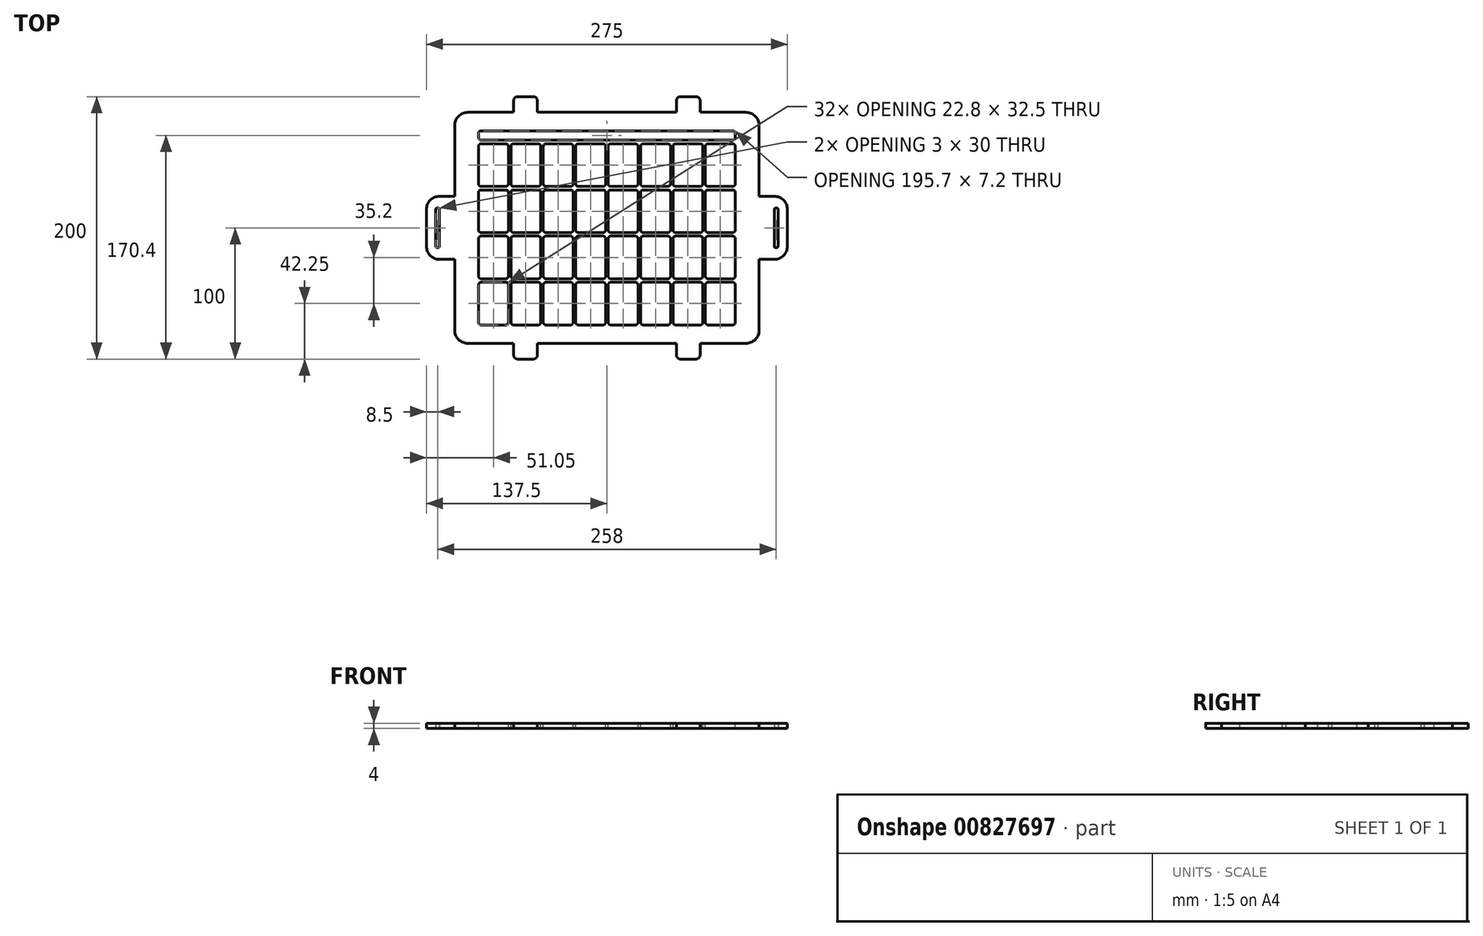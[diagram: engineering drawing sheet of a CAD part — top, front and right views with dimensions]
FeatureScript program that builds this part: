
annotation { "Feature Type Name" : "Feature", "Feature Type Description" : "" }
export const myFeature = defineFeature(function(context is Context, id is Id, definition is map)
    precondition{}
    {
        {
            var Q0;
            Q0=qCreatedBy(makeId("Top.planeOp"),FACE);
            var sketch = newSketch(context, id + "F0", { "sketchPlane" : qUnion([Q0])});
            skLineSegment(sketch, "E0", {"start": v(0, 0) * mm, "end": v(137.5, 0) * mm, "construction": true});
            skLineSegment(sketch, "E1", {"start": v(0, 0) * mm, "end": v(0, 88) * mm, "construction": true});
            skLineSegment(sketch, "E2.MirrorCS", {"start": v(0, 0) * mm, "end": v(0, -88) * mm, "construction": true});
            skLineSegment(sketch, "E3.MirrorCS", {"start": v(0, 0) * mm, "end": v(-137.5, 0) * mm, "construction": true});
            skLineSegment(sketch, "E4.bottom", {"start": v(106, -88) * mm, "end": v(71, -88) * mm});
            skLineSegment(sketch, "E4.top", {"start": v(106, 88) * mm, "end": v(71, 88) * mm});
            skLineSegment(sketch, "E4.left", {"start": v(116, -78) * mm, "end": v(116, -24) * mm});
            skLineSegment(sketch, "E4.right", {"start": v(-116, -78) * mm, "end": v(-116, -24) * mm});
            skPoint(sketch, "E4.middle", {"position": v(0, 0) * mm});
            skLineSegment(sketch, "E5", {"start": v(68, 100) * mm, "end": v(56, 100) * mm});
            skPoint(sketch, "E6.orphan", {"position": v(53, 88) * mm});
            skLineSegment(sketch, "E7", {"start": v(71, 97) * mm, "end": v(71, 88) * mm});
            skLineSegment(sketch, "E8.trimOffspring", {"start": v(53, 88) * mm, "end": v(-53, 88) * mm});
            skLineSegment(sketch, "E9.MirrorCS", {"start": v(68, -100) * mm, "end": v(56, -100) * mm});
            skLineSegment(sketch, "E10.MirrorCS", {"start": v(71, -97) * mm, "end": v(71, -88) * mm});
            skLineSegment(sketch, "E11.trimOffspring", {"start": v(53, -88) * mm, "end": v(-53, -88) * mm});
            skLineSegment(sketch, "E12.MirrorCS", {"start": v(-68, -100) * mm, "end": v(-56, -100) * mm});
            skLineSegment(sketch, "E13.MirrorCS", {"start": v(-71, -97) * mm, "end": v(-71, -88) * mm});
            skLineSegment(sketch, "E14.MirrorCS", {"start": v(-68, 100) * mm, "end": v(-56, 100) * mm});
            skLineSegment(sketch, "E15.MirrorCS", {"start": v(-71, 97) * mm, "end": v(-71, 88) * mm});
            skLineSegment(sketch, "E16", {"start": v(-53, -97) * mm, "end": v(-53, -88) * mm});
            skLineSegment(sketch, "E17.trimOffspring", {"start": v(-71, -88) * mm, "end": v(-106, -88) * mm});
            skLineSegment(sketch, "E18", {"start": v(-53, 97) * mm, "end": v(-53, 88) * mm});
            skLineSegment(sketch, "E19.trimOffspring", {"start": v(-71, 88) * mm, "end": v(-106, 88) * mm});
            skLineSegment(sketch, "E20", {"start": v(53, 97) * mm, "end": v(53, 88) * mm});
            skLineSegment(sketch, "E21", {"start": v(53, -97) * mm, "end": v(53, -88) * mm});
            skPoint(sketch, "E22.visualSharp", {"position": v(-71, 100) * mm});
            skArc(sketch, "E22.filletArc", {"start": v(-68, 100) * mm, "mid": v(-70.12, 99.12) * mm, "end": v(-71, 97) * mm});
            skPoint(sketch, "E23.visualSharp", {"position": v(-53, 100) * mm});
            skArc(sketch, "E23.filletArc", {"start": v(-53, 97) * mm, "mid": v(-53.88, 99.12) * mm, "end": v(-56, 100) * mm});
            skPoint(sketch, "E24.visualSharp", {"position": v(53, 100) * mm});
            skArc(sketch, "E24.filletArc", {"start": v(56, 100) * mm, "mid": v(53.88, 99.12) * mm, "end": v(53, 97) * mm});
            skPoint(sketch, "E25.visualSharp", {"position": v(71, 100) * mm});
            skArc(sketch, "E25.filletArc", {"start": v(71, 97) * mm, "mid": v(70.12, 99.12) * mm, "end": v(68, 100) * mm});
            skPoint(sketch, "E26.visualSharp", {"position": v(-71, -100) * mm});
            skArc(sketch, "E26.filletArc", {"start": v(-71, -97) * mm, "mid": v(-70.12, -99.12) * mm, "end": v(-68, -100) * mm});
            skPoint(sketch, "E27.visualSharp", {"position": v(-53, -100) * mm});
            skArc(sketch, "E27.filletArc", {"start": v(-56, -100) * mm, "mid": v(-53.88, -99.12) * mm, "end": v(-53, -97) * mm});
            skPoint(sketch, "E28.visualSharp", {"position": v(53, -100) * mm});
            skArc(sketch, "E28.filletArc", {"start": v(53, -97) * mm, "mid": v(53.88, -99.12) * mm, "end": v(56, -100) * mm});
            skPoint(sketch, "E29.visualSharp", {"position": v(71, -100) * mm});
            skArc(sketch, "E29.filletArc", {"start": v(68, -100) * mm, "mid": v(70.12, -99.12) * mm, "end": v(71, -97) * mm});
            skLineSegment(sketch, "E30", {"start": v(137.5, -14) * mm, "end": v(137.5, 14) * mm});
            skLineSegment(sketch, "E31", {"start": v(127.5, 24) * mm, "end": v(116, 24) * mm});
            skLineSegment(sketch, "E32.MirrorCS", {"start": v(127.5, -24) * mm, "end": v(116, -24) * mm});
            skPoint(sketch, "E33.orphan", {"position": v(137.5, 53.3) * mm});
            skLineSegment(sketch, "E34.trimOffspring", {"start": v(116, 24) * mm, "end": v(116, 78) * mm});
            skPoint(sketch, "E35.orphan", {"position": v(0, 24) * mm});
            skPoint(sketch, "E36.orphan", {"position": v(0, -24) * mm});
            skPoint(sketch, "E37.visualSharp", {"position": v(137.5, 24) * mm});
            skArc(sketch, "E37.filletArc", {"start": v(137.5, 14) * mm, "mid": v(134.57, 21.07) * mm, "end": v(127.5, 24) * mm});
            skPoint(sketch, "E38.visualSharp", {"position": v(137.5, -24) * mm});
            skArc(sketch, "E38.filletArc", {"start": v(127.5, -24) * mm, "mid": v(134.57, -21.07) * mm, "end": v(137.5, -14) * mm});
            skLineSegment(sketch, "E39", {"start": v(127.5, 15) * mm, "end": v(130.5, 15) * mm});
            skPoint(sketch, "E40.trimOffspring.end.orphan", {"position": v(146.66, 15) * mm});
            skLineSegment(sketch, "E41.MirrorCS", {"start": v(127.5, -15) * mm, "end": v(130.5, -15) * mm});
            skLineSegment(sketch, "E42.MirrorCS", {"start": v(-127.5, 24) * mm, "end": v(-116, 24) * mm});
            skArc(sketch, "E43.MirrorCS", {"start": v(-137.5, 14) * mm, "mid": v(-134.57, 21.07) * mm, "end": v(-127.5, 24) * mm});
            skLineSegment(sketch, "E44.MirrorCS", {"start": v(-137.5, -14) * mm, "end": v(-137.5, 14) * mm});
            skArc(sketch, "E45.MirrorCS", {"start": v(-127.5, -24) * mm, "mid": v(-134.57, -21.07) * mm, "end": v(-137.5, -14) * mm});
            skLineSegment(sketch, "E46.MirrorCS", {"start": v(-127.5, -24) * mm, "end": v(-116, -24) * mm});
            skLineSegment(sketch, "E47.MirrorCS", {"start": v(-127.5, 0) * mm, "end": v(-127.5, 15) * mm});
            skLineSegment(sketch, "E48.MirrorCS", {"start": v(-130.5, 0) * mm, "end": v(-130.5, 15) * mm});
            skLineSegment(sketch, "E49.MirrorCS", {"start": v(-130.5, 0) * mm, "end": v(-130.5, -15) * mm});
            skLineSegment(sketch, "E50.MirrorCS", {"start": v(-127.5, 0) * mm, "end": v(-127.5, -15) * mm});
            skLineSegment(sketch, "E51.MirrorCS", {"start": v(-127.5, 15) * mm, "end": v(-130.5, 15) * mm});
            skLineSegment(sketch, "E52.MirrorCS", {"start": v(-127.5, -15) * mm, "end": v(-130.5, -15) * mm});
            skLineSegment(sketch, "E53.trimOffspring", {"start": v(-116, 24) * mm, "end": v(-116, 78) * mm});
            skPoint(sketch, "E54.visualSharp", {"position": v(-116, 88) * mm});
            skArc(sketch, "E54.filletArc", {"start": v(-106, 88) * mm, "mid": v(-113.07, 85.07) * mm, "end": v(-116, 78) * mm});
            skPoint(sketch, "E55.visualSharp", {"position": v(-116, -88) * mm});
            skArc(sketch, "E55.filletArc", {"start": v(-116, -78) * mm, "mid": v(-113.07, -85.07) * mm, "end": v(-106, -88) * mm});
            skPoint(sketch, "E56.visualSharp", {"position": v(116, -88) * mm});
            skArc(sketch, "E56.filletArc", {"start": v(106, -88) * mm, "mid": v(113.07, -85.07) * mm, "end": v(116, -78) * mm});
            skPoint(sketch, "E57.visualSharp", {"position": v(116, 88) * mm});
            skArc(sketch, "E57.filletArc", {"start": v(116, 78) * mm, "mid": v(113.07, 85.07) * mm, "end": v(106, 88) * mm});
            skLineSegment(sketch, "E58", {"start": v(127.5, -15) * mm, "end": v(127.5, 15) * mm});
            skLineSegment(sketch, "E59", {"start": v(130.5, -15) * mm, "end": v(130.5, 15) * mm});
            skSolve(sketch);
        }
        {
            var Q0;
            Q0=qSketchRegion(id+"F0",true);
            extrude(context, id + "F1", {"entities" : qUnion([Q0]), "depth" : 4 * mm, "offsetDistance" : 25 * mm});
        }
        {
            var Q0;
            Q0=makeQuery(id+"F1.opExtrude","SWEPT_EDGE",EDGE,{"disambiguationData":[OSD([sQuery(id+"F0.wireOp",EDGE,"E41.MirrorCS"),sQuery(id+"F0.wireOp",EDGE,"E58")])]});
            var Q1;
            Q1=makeQuery(id+"F1.opExtrude","SWEPT_EDGE",EDGE,{"disambiguationData":[OSD([sQuery(id+"F0.wireOp",EDGE,"E41.MirrorCS"),sQuery(id+"F0.wireOp",EDGE,"E59")])]});
            fillet(context, id + "F2", {"entities" : qUnion([Q0, Q1]), "radius" : 1 * mm, "tangentPropagation" : true, "allowEdgeOverflow" : false});
        }
        {
            var Q0;
            Q0=makeQuery(id+"F1.opExtrude","SWEPT_EDGE",EDGE,{"disambiguationData":[OSD([sQuery(id+"F0.wireOp",EDGE,"E39"),sQuery(id+"F0.wireOp",EDGE,"E58")])]});
            var Q1;
            Q1=makeQuery(id+"F1.opExtrude","SWEPT_EDGE",EDGE,{"disambiguationData":[OSD([sQuery(id+"F0.wireOp",EDGE,"E39"),sQuery(id+"F0.wireOp",EDGE,"E59")])]});
            fillet(context, id + "F3", {"entities" : qUnion([Q0, Q1]), "radius" : 1 * mm, "tangentPropagation" : true, "allowEdgeOverflow" : false});
        }
        {
            var Q0;
            Q0=makeQuery(id+"F1.opExtrude","SWEPT_EDGE",EDGE,{"disambiguationData":[OSD([sQuery(id+"F0.wireOp",EDGE,"E48.MirrorCS"),sQuery(id+"F0.wireOp",EDGE,"E51.MirrorCS")])]});
            var Q1;
            Q1=makeQuery(id+"F1.opExtrude","SWEPT_EDGE",EDGE,{"disambiguationData":[OSD([sQuery(id+"F0.wireOp",EDGE,"E47.MirrorCS"),sQuery(id+"F0.wireOp",EDGE,"E51.MirrorCS")])]});
            fillet(context, id + "F4", {"entities" : qUnion([Q0, Q1]), "radius" : 1 * mm, "tangentPropagation" : true, "allowEdgeOverflow" : false});
        }
        {
            var Q0;
            Q0=makeQuery(id+"F1.opExtrude","SWEPT_EDGE",EDGE,{"disambiguationData":[OSD([sQuery(id+"F0.wireOp",EDGE,"E49.MirrorCS"),sQuery(id+"F0.wireOp",EDGE,"E52.MirrorCS")])]});
            var Q1;
            Q1=makeQuery(id+"F1.opExtrude","SWEPT_EDGE",EDGE,{"disambiguationData":[OSD([sQuery(id+"F0.wireOp",EDGE,"E50.MirrorCS"),sQuery(id+"F0.wireOp",EDGE,"E52.MirrorCS")])]});
            fillet(context, id + "F5", {"entities" : qUnion([Q0, Q1]), "radius" : 1 * mm, "tangentPropagation" : true, "allowEdgeOverflow" : false});
        }
        {
            var Q0;
            Q0=makeQuery(id+"F1.opExtrude","CAP_FACE",FACE,{"disambiguationData":[OSD([sQuery(id+"F0.wireOp",EDGE,"E4.bottom"),sQuery(id+"F0.wireOp",EDGE,"E4.top"),sQuery(id+"F0.wireOp",EDGE,"E4.left"),sQuery(id+"F0.wireOp",EDGE,"E4.right"),sQuery(id+"F0.wireOp",EDGE,"E5"),sQuery(id+"F0.wireOp",EDGE,"E7"),sQuery(id+"F0.wireOp",EDGE,"E8.trimOffspring"),sQuery(id+"F0.wireOp",EDGE,"E9.MirrorCS"),sQuery(id+"F0.wireOp",EDGE,"E10.MirrorCS"),sQuery(id+"F0.wireOp",EDGE,"E11.trimOffspring"),sQuery(id+"F0.wireOp",EDGE,"E12.MirrorCS"),sQuery(id+"F0.wireOp",EDGE,"E13.MirrorCS"),sQuery(id+"F0.wireOp",EDGE,"E14.MirrorCS"),sQuery(id+"F0.wireOp",EDGE,"E15.MirrorCS"),sQuery(id+"F0.wireOp",EDGE,"E16"),sQuery(id+"F0.wireOp",EDGE,"E17.trimOffspring"),sQuery(id+"F0.wireOp",EDGE,"E18"),sQuery(id+"F0.wireOp",EDGE,"E19.trimOffspring"),sQuery(id+"F0.wireOp",EDGE,"E20"),sQuery(id+"F0.wireOp",EDGE,"E21"),sQuery(id+"F0.wireOp",EDGE,"E22.filletArc"),sQuery(id+"F0.wireOp",EDGE,"E23.filletArc"),sQuery(id+"F0.wireOp",EDGE,"E24.filletArc"),sQuery(id+"F0.wireOp",EDGE,"E25.filletArc"),sQuery(id+"F0.wireOp",EDGE,"E26.filletArc"),sQuery(id+"F0.wireOp",EDGE,"E27.filletArc"),sQuery(id+"F0.wireOp",EDGE,"E28.filletArc"),sQuery(id+"F0.wireOp",EDGE,"E29.filletArc"),sQuery(id+"F0.wireOp",EDGE,"E30"),sQuery(id+"F0.wireOp",EDGE,"E31"),sQuery(id+"F0.wireOp",EDGE,"E32.MirrorCS"),sQuery(id+"F0.wireOp",EDGE,"E34.trimOffspring"),sQuery(id+"F0.wireOp",EDGE,"E37.filletArc"),sQuery(id+"F0.wireOp",EDGE,"E38.filletArc"),sQuery(id+"F0.wireOp",EDGE,"E39"),sQuery(id+"F0.wireOp",EDGE,"E41.MirrorCS"),sQuery(id+"F0.wireOp",EDGE,"E42.MirrorCS"),sQuery(id+"F0.wireOp",EDGE,"E43.MirrorCS"),sQuery(id+"F0.wireOp",EDGE,"E44.MirrorCS"),sQuery(id+"F0.wireOp",EDGE,"E45.MirrorCS"),sQuery(id+"F0.wireOp",EDGE,"E46.MirrorCS"),sQuery(id+"F0.wireOp",EDGE,"E47.MirrorCS"),sQuery(id+"F0.wireOp",EDGE,"E48.MirrorCS"),sQuery(id+"F0.wireOp",EDGE,"E49.MirrorCS"),sQuery(id+"F0.wireOp",EDGE,"E50.MirrorCS"),sQuery(id+"F0.wireOp",EDGE,"E51.MirrorCS"),sQuery(id+"F0.wireOp",EDGE,"E52.MirrorCS"),sQuery(id+"F0.wireOp",EDGE,"E53.trimOffspring"),sQuery(id+"F0.wireOp",EDGE,"E54.filletArc"),sQuery(id+"F0.wireOp",EDGE,"E55.filletArc"),sQuery(id+"F0.wireOp",EDGE,"E56.filletArc"),sQuery(id+"F0.wireOp",EDGE,"E57.filletArc"),sQuery(id+"F0.wireOp",EDGE,"E58"),sQuery(id+"F0.wireOp",EDGE,"E59")])],"isStart":false});
            var sketch = newSketch(context, id + "F6", { "sketchPlane" : qUnion([Q0])});
            skLineSegment(sketch, "E60", {"start": v(-127.5, 0) * mm, "end": v(127.5, 0) * mm, "construction": true});
            skLineSegment(sketch, "E61.bottom", {"start": v(95.85, 74) * mm, "end": v(-95.85, 74) * mm});
            skPoint(sketch, "E61.middle", {"position": v(0, 0) * mm});
            skLineSegment(sketch, "E62.bottom", {"start": v(-95.85, -74) * mm, "end": v(-77.05, -74) * mm});
            skLineSegment(sketch, "E62.top", {"start": v(-95.85, -41.5) * mm, "end": v(-77.05, -41.5) * mm});
            skLineSegment(sketch, "E62.left", {"start": v(-97.85, -72) * mm, "end": v(-97.85, -43.5) * mm});
            skLineSegment(sketch, "E62.right", {"start": v(-75.05, -72) * mm, "end": v(-75.05, -43.5) * mm});
            skPoint(sketch, "E63.visualSharp", {"position": v(-75.05, -41.5) * mm});
            skArc(sketch, "E63.filletArc", {"start": v(-75.05, -43.5) * mm, "mid": v(-75.64, -42.09) * mm, "end": v(-77.05, -41.5) * mm});
            skPoint(sketch, "E64.visualSharp", {"position": v(-75.05, -74) * mm});
            skArc(sketch, "E64.filletArc", {"start": v(-77.05, -74) * mm, "mid": v(-75.64, -73.41) * mm, "end": v(-75.05, -72) * mm});
            skPoint(sketch, "E65.visualSharp", {"position": v(-97.85, -74) * mm});
            skArc(sketch, "E65.filletArc", {"start": v(-97.85, -72) * mm, "mid": v(-97.26, -73.41) * mm, "end": v(-95.85, -74) * mm});
            skPoint(sketch, "E66.visualSharp", {"position": v(-97.85, -41.5) * mm});
            skArc(sketch, "E66.filletArc", {"start": v(-95.85, -41.5) * mm, "mid": v(-97.26, -42.09) * mm, "end": v(-97.85, -43.5) * mm});
            skPoint(sketch, "E67.1.0.0", {"position": v(-50.35, -74) * mm});
            skPoint(sketch, "E67.1.0.1", {"position": v(-73.15, -41.5) * mm});
            skPoint(sketch, "E67.1.0.2", {"position": v(-73.15, -74) * mm});
            skLineSegment(sketch, "E67.1.0.3", {"start": v(-71.15, -74) * mm, "end": v(-52.35, -74) * mm});
            skLineSegment(sketch, "E67.1.0.4", {"start": v(-50.35, -72) * mm, "end": v(-50.35, -43.5) * mm});
            skPoint(sketch, "E67.1.0.5", {"position": v(-50.35, -41.5) * mm});
            skLineSegment(sketch, "E67.1.0.6", {"start": v(-71.15, -41.5) * mm, "end": v(-52.35, -41.5) * mm});
            skLineSegment(sketch, "E67.1.0.7", {"start": v(-73.15, -72) * mm, "end": v(-73.15, -43.5) * mm});
            skPoint(sketch, "E67.1.0.8", {"position": v(-73.15, -74) * mm});
            skArc(sketch, "E67.1.0.9", {"start": v(-52.35, -74) * mm, "mid": v(-50.94, -73.41) * mm, "end": v(-50.35, -72) * mm});
            skArc(sketch, "E67.1.0.10", {"start": v(-50.35, -43.5) * mm, "mid": v(-50.94, -42.09) * mm, "end": v(-52.35, -41.5) * mm});
            skArc(sketch, "E67.1.0.11", {"start": v(-71.15, -41.5) * mm, "mid": v(-72.56, -42.09) * mm, "end": v(-73.15, -43.5) * mm});
            skArc(sketch, "E67.1.0.12", {"start": v(-73.15, -72) * mm, "mid": v(-72.56, -73.41) * mm, "end": v(-71.15, -74) * mm});
            skArc(sketch, "E67.1.0.13", {"start": v(-73.15, -72) * mm, "mid": v(-72.56, -73.41) * mm, "end": v(-71.15, -74) * mm});
            skPoint(sketch, "E67.2.0.0", {"position": v(-25.65, -74) * mm});
            skPoint(sketch, "E67.2.0.1", {"position": v(-48.45, -41.5) * mm});
            skPoint(sketch, "E67.2.0.2", {"position": v(-48.45, -74) * mm});
            skLineSegment(sketch, "E67.2.0.3", {"start": v(-46.45, -74) * mm, "end": v(-27.65, -74) * mm});
            skLineSegment(sketch, "E67.2.0.4", {"start": v(-25.65, -72) * mm, "end": v(-25.65, -43.5) * mm});
            skPoint(sketch, "E67.2.0.5", {"position": v(-25.65, -41.5) * mm});
            skLineSegment(sketch, "E67.2.0.6", {"start": v(-46.45, -41.5) * mm, "end": v(-27.65, -41.5) * mm});
            skLineSegment(sketch, "E67.2.0.7", {"start": v(-48.45, -72) * mm, "end": v(-48.45, -43.5) * mm});
            skPoint(sketch, "E67.2.0.8", {"position": v(-48.45, -74) * mm});
            skArc(sketch, "E67.2.0.9", {"start": v(-27.65, -74) * mm, "mid": v(-26.24, -73.41) * mm, "end": v(-25.65, -72) * mm});
            skArc(sketch, "E67.2.0.10", {"start": v(-25.65, -43.5) * mm, "mid": v(-26.24, -42.09) * mm, "end": v(-27.65, -41.5) * mm});
            skArc(sketch, "E67.2.0.11", {"start": v(-46.45, -41.5) * mm, "mid": v(-47.86, -42.09) * mm, "end": v(-48.45, -43.5) * mm});
            skArc(sketch, "E67.2.0.12", {"start": v(-48.45, -72) * mm, "mid": v(-47.86, -73.41) * mm, "end": v(-46.45, -74) * mm});
            skArc(sketch, "E67.2.0.13", {"start": v(-48.45, -72) * mm, "mid": v(-47.86, -73.41) * mm, "end": v(-46.45, -74) * mm});
            skPoint(sketch, "E67.3.0.0", {"position": v(-0.95, -74) * mm});
            skPoint(sketch, "E67.3.0.1", {"position": v(-23.75, -41.5) * mm});
            skPoint(sketch, "E67.3.0.2", {"position": v(-23.75, -74) * mm});
            skLineSegment(sketch, "E67.3.0.3", {"start": v(-21.75, -74) * mm, "end": v(-2.95, -74) * mm});
            skLineSegment(sketch, "E67.3.0.4", {"start": v(-0.95, -72) * mm, "end": v(-0.95, -43.5) * mm});
            skPoint(sketch, "E67.3.0.5", {"position": v(-0.95, -41.5) * mm});
            skLineSegment(sketch, "E67.3.0.6", {"start": v(-21.75, -41.5) * mm, "end": v(-2.95, -41.5) * mm});
            skLineSegment(sketch, "E67.3.0.7", {"start": v(-23.75, -72) * mm, "end": v(-23.75, -43.5) * mm});
            skPoint(sketch, "E67.3.0.8", {"position": v(-23.75, -74) * mm});
            skArc(sketch, "E67.3.0.9", {"start": v(-2.95, -74) * mm, "mid": v(-1.54, -73.41) * mm, "end": v(-0.95, -72) * mm});
            skArc(sketch, "E67.3.0.10", {"start": v(-0.95, -43.5) * mm, "mid": v(-1.54, -42.09) * mm, "end": v(-2.95, -41.5) * mm});
            skArc(sketch, "E67.3.0.11", {"start": v(-21.75, -41.5) * mm, "mid": v(-23.16, -42.09) * mm, "end": v(-23.75, -43.5) * mm});
            skArc(sketch, "E67.3.0.12", {"start": v(-23.75, -72) * mm, "mid": v(-23.16, -73.41) * mm, "end": v(-21.75, -74) * mm});
            skArc(sketch, "E67.3.0.13", {"start": v(-23.75, -72) * mm, "mid": v(-23.16, -73.41) * mm, "end": v(-21.75, -74) * mm});
            skPoint(sketch, "E67.4.0.0", {"position": v(23.75, -74) * mm});
            skPoint(sketch, "E67.4.0.1", {"position": v(0.95, -41.5) * mm});
            skPoint(sketch, "E67.4.0.2", {"position": v(0.95, -74) * mm});
            skLineSegment(sketch, "E67.4.0.3", {"start": v(2.95, -74) * mm, "end": v(21.75, -74) * mm});
            skLineSegment(sketch, "E67.4.0.4", {"start": v(23.75, -72) * mm, "end": v(23.75, -43.5) * mm});
            skPoint(sketch, "E67.4.0.5", {"position": v(23.75, -41.5) * mm});
            skLineSegment(sketch, "E67.4.0.6", {"start": v(2.95, -41.5) * mm, "end": v(21.75, -41.5) * mm});
            skLineSegment(sketch, "E67.4.0.7", {"start": v(0.95, -72) * mm, "end": v(0.95, -43.5) * mm});
            skPoint(sketch, "E67.4.0.8", {"position": v(0.95, -74) * mm});
            skArc(sketch, "E67.4.0.9", {"start": v(21.75, -74) * mm, "mid": v(23.16, -73.41) * mm, "end": v(23.75, -72) * mm});
            skArc(sketch, "E67.4.0.10", {"start": v(23.75, -43.5) * mm, "mid": v(23.16, -42.09) * mm, "end": v(21.75, -41.5) * mm});
            skArc(sketch, "E67.4.0.11", {"start": v(2.95, -41.5) * mm, "mid": v(1.54, -42.09) * mm, "end": v(0.95, -43.5) * mm});
            skArc(sketch, "E67.4.0.12", {"start": v(0.95, -72) * mm, "mid": v(1.54, -73.41) * mm, "end": v(2.95, -74) * mm});
            skArc(sketch, "E67.4.0.13", {"start": v(0.95, -72) * mm, "mid": v(1.54, -73.41) * mm, "end": v(2.95, -74) * mm});
            skPoint(sketch, "E67.5.0.0", {"position": v(48.45, -74) * mm});
            skPoint(sketch, "E67.5.0.1", {"position": v(25.65, -41.5) * mm});
            skPoint(sketch, "E67.5.0.2", {"position": v(25.65, -74) * mm});
            skLineSegment(sketch, "E67.5.0.3", {"start": v(27.65, -74) * mm, "end": v(46.45, -74) * mm});
            skLineSegment(sketch, "E67.5.0.4", {"start": v(48.45, -72) * mm, "end": v(48.45, -43.5) * mm});
            skPoint(sketch, "E67.5.0.5", {"position": v(48.45, -41.5) * mm});
            skLineSegment(sketch, "E67.5.0.6", {"start": v(27.65, -41.5) * mm, "end": v(46.45, -41.5) * mm});
            skLineSegment(sketch, "E67.5.0.7", {"start": v(25.65, -72) * mm, "end": v(25.65, -43.5) * mm});
            skPoint(sketch, "E67.5.0.8", {"position": v(25.65, -74) * mm});
            skArc(sketch, "E67.5.0.9", {"start": v(46.45, -74) * mm, "mid": v(47.86, -73.41) * mm, "end": v(48.45, -72) * mm});
            skArc(sketch, "E67.5.0.10", {"start": v(48.45, -43.5) * mm, "mid": v(47.86, -42.09) * mm, "end": v(46.45, -41.5) * mm});
            skArc(sketch, "E67.5.0.11", {"start": v(27.65, -41.5) * mm, "mid": v(26.24, -42.09) * mm, "end": v(25.65, -43.5) * mm});
            skArc(sketch, "E67.5.0.12", {"start": v(25.65, -72) * mm, "mid": v(26.24, -73.41) * mm, "end": v(27.65, -74) * mm});
            skArc(sketch, "E67.5.0.13", {"start": v(25.65, -72) * mm, "mid": v(26.24, -73.41) * mm, "end": v(27.65, -74) * mm});
            skPoint(sketch, "E67.6.0.0", {"position": v(73.15, -74) * mm});
            skPoint(sketch, "E67.6.0.1", {"position": v(50.35, -41.5) * mm});
            skPoint(sketch, "E67.6.0.2", {"position": v(50.35, -74) * mm});
            skLineSegment(sketch, "E67.6.0.3", {"start": v(52.35, -74) * mm, "end": v(71.15, -74) * mm});
            skLineSegment(sketch, "E67.6.0.4", {"start": v(73.15, -72) * mm, "end": v(73.15, -43.5) * mm});
            skPoint(sketch, "E67.6.0.5", {"position": v(73.15, -41.5) * mm});
            skLineSegment(sketch, "E67.6.0.6", {"start": v(52.35, -41.5) * mm, "end": v(71.15, -41.5) * mm});
            skLineSegment(sketch, "E67.6.0.7", {"start": v(50.35, -72) * mm, "end": v(50.35, -43.5) * mm});
            skPoint(sketch, "E67.6.0.8", {"position": v(50.35, -74) * mm});
            skArc(sketch, "E67.6.0.9", {"start": v(71.15, -74) * mm, "mid": v(72.56, -73.41) * mm, "end": v(73.15, -72) * mm});
            skArc(sketch, "E67.6.0.10", {"start": v(73.15, -43.5) * mm, "mid": v(72.56, -42.09) * mm, "end": v(71.15, -41.5) * mm});
            skArc(sketch, "E67.6.0.11", {"start": v(52.35, -41.5) * mm, "mid": v(50.94, -42.09) * mm, "end": v(50.35, -43.5) * mm});
            skArc(sketch, "E67.6.0.12", {"start": v(50.35, -72) * mm, "mid": v(50.94, -73.41) * mm, "end": v(52.35, -74) * mm});
            skArc(sketch, "E67.6.0.13", {"start": v(50.35, -72) * mm, "mid": v(50.94, -73.41) * mm, "end": v(52.35, -74) * mm});
            skPoint(sketch, "E67.7.0.0", {"position": v(97.85, -74) * mm});
            skPoint(sketch, "E67.7.0.1", {"position": v(75.05, -41.5) * mm});
            skPoint(sketch, "E67.7.0.2", {"position": v(75.05, -74) * mm});
            skLineSegment(sketch, "E67.7.0.3", {"start": v(77.05, -74) * mm, "end": v(95.85, -74) * mm});
            skLineSegment(sketch, "E67.7.0.4", {"start": v(97.85, -72) * mm, "end": v(97.85, -43.5) * mm});
            skPoint(sketch, "E67.7.0.5", {"position": v(97.85, -41.5) * mm});
            skLineSegment(sketch, "E67.7.0.6", {"start": v(77.05, -41.5) * mm, "end": v(95.85, -41.5) * mm});
            skLineSegment(sketch, "E67.7.0.7", {"start": v(75.05, -72) * mm, "end": v(75.05, -43.5) * mm});
            skPoint(sketch, "E67.7.0.8", {"position": v(75.05, -74) * mm});
            skArc(sketch, "E67.7.0.9", {"start": v(95.85, -74) * mm, "mid": v(97.26, -73.41) * mm, "end": v(97.85, -72) * mm});
            skArc(sketch, "E67.7.0.10", {"start": v(97.85, -43.5) * mm, "mid": v(97.26, -42.09) * mm, "end": v(95.85, -41.5) * mm});
            skArc(sketch, "E67.7.0.11", {"start": v(77.05, -41.5) * mm, "mid": v(75.64, -42.09) * mm, "end": v(75.05, -43.5) * mm});
            skArc(sketch, "E67.7.0.12", {"start": v(75.05, -72) * mm, "mid": v(75.64, -73.41) * mm, "end": v(77.05, -74) * mm});
            skArc(sketch, "E67.7.0.13", {"start": v(75.05, -72) * mm, "mid": v(75.64, -73.41) * mm, "end": v(77.05, -74) * mm});
            skLineSegment(sketch, "E67.direction1", {"start": v(-97.85, -74) * mm, "end": v(-73.15, -74) * mm, "construction": true});
            skLineSegment(sketch, "E68.0.1.0", {"start": v(-25.65, -36.8) * mm, "end": v(-25.65, -8.3) * mm});
            skPoint(sketch, "E68.0.1.1", {"position": v(25.65, -38.8) * mm});
            skLineSegment(sketch, "E68.0.1.2", {"start": v(-75.05, -36.8) * mm, "end": v(-75.05, -8.3) * mm});
            skPoint(sketch, "E68.0.1.3", {"position": v(75.05, -6.3) * mm});
            skPoint(sketch, "E68.0.1.4", {"position": v(-50.35, -38.8) * mm});
            skLineSegment(sketch, "E68.0.1.5", {"start": v(27.65, -6.3) * mm, "end": v(46.45, -6.3) * mm});
            skLineSegment(sketch, "E68.0.1.6", {"start": v(48.45, -36.8) * mm, "end": v(48.45, -8.3) * mm});
            skPoint(sketch, "E68.0.1.7", {"position": v(0.95, -6.3) * mm});
            skPoint(sketch, "E68.0.1.8", {"position": v(-73.15, -38.8) * mm});
            skLineSegment(sketch, "E68.0.1.9", {"start": v(-95.85, -6.3) * mm, "end": v(-77.05, -6.3) * mm});
            skLineSegment(sketch, "E68.0.1.10", {"start": v(-97.85, -36.8) * mm, "end": v(-97.85, -8.3) * mm});
            skLineSegment(sketch, "E68.0.1.11", {"start": v(75.05, -36.8) * mm, "end": v(75.05, -8.3) * mm});
            skLineSegment(sketch, "E68.0.1.12", {"start": v(-21.75, -38.8) * mm, "end": v(-2.95, -38.8) * mm});
            skPoint(sketch, "E68.0.1.13", {"position": v(50.35, -6.3) * mm});
            skPoint(sketch, "E68.0.1.14", {"position": v(97.85, -6.3) * mm});
            skPoint(sketch, "E68.0.1.15", {"position": v(-97.85, -6.3) * mm});
            skLineSegment(sketch, "E68.0.1.16", {"start": v(-23.75, -36.8) * mm, "end": v(-23.75, -8.3) * mm});
            skPoint(sketch, "E68.0.1.17", {"position": v(-0.95, -38.8) * mm});
            skPoint(sketch, "E68.0.1.18", {"position": v(-25.65, -6.3) * mm});
            skPoint(sketch, "E68.0.1.19", {"position": v(-25.65, -38.8) * mm});
            skLineSegment(sketch, "E68.0.1.20", {"start": v(-71.15, -6.3) * mm, "end": v(-52.35, -6.3) * mm});
            skPoint(sketch, "E68.0.1.21", {"position": v(97.85, -38.8) * mm});
            skPoint(sketch, "E68.0.1.22", {"position": v(-75.05, -6.3) * mm});
            skPoint(sketch, "E68.0.1.23", {"position": v(50.35, -38.8) * mm});
            skPoint(sketch, "E68.0.1.24", {"position": v(-48.45, -6.3) * mm});
            skLineSegment(sketch, "E68.0.1.25", {"start": v(2.95, -6.3) * mm, "end": v(21.75, -6.3) * mm});
            skPoint(sketch, "E68.0.1.26", {"position": v(-50.35, -6.3) * mm});
            skLineSegment(sketch, "E68.0.1.27", {"start": v(2.95, -38.8) * mm, "end": v(21.75, -38.8) * mm});
            skLineSegment(sketch, "E68.0.1.28", {"start": v(-73.15, -36.8) * mm, "end": v(-73.15, -8.3) * mm});
            skLineSegment(sketch, "E68.0.1.29", {"start": v(-46.45, -6.3) * mm, "end": v(-27.65, -6.3) * mm});
            skLineSegment(sketch, "E68.0.1.30", {"start": v(23.75, -36.8) * mm, "end": v(23.75, -8.3) * mm});
            skLineSegment(sketch, "E68.0.1.31", {"start": v(50.35, -36.8) * mm, "end": v(50.35, -8.3) * mm});
            skLineSegment(sketch, "E68.0.1.32", {"start": v(-46.45, -38.8) * mm, "end": v(-27.65, -38.8) * mm});
            skPoint(sketch, "E68.0.1.33", {"position": v(48.45, -6.3) * mm});
            skLineSegment(sketch, "E68.0.1.34", {"start": v(52.35, -38.8) * mm, "end": v(71.15, -38.8) * mm});
            skLineSegment(sketch, "E68.0.1.35", {"start": v(-0.95, -36.8) * mm, "end": v(-0.95, -8.3) * mm});
            skLineSegment(sketch, "E68.0.1.36", {"start": v(-48.45, -36.8) * mm, "end": v(-48.45, -8.3) * mm});
            skLineSegment(sketch, "E68.0.1.37", {"start": v(77.05, -6.3) * mm, "end": v(95.85, -6.3) * mm});
            skPoint(sketch, "E68.0.1.38", {"position": v(0.95, -38.8) * mm});
            skPoint(sketch, "E68.0.1.39", {"position": v(25.65, -6.3) * mm});
            skLineSegment(sketch, "E68.0.1.40", {"start": v(52.35, -6.3) * mm, "end": v(71.15, -6.3) * mm});
            skLineSegment(sketch, "E68.0.1.41", {"start": v(97.85, -36.8) * mm, "end": v(97.85, -8.3) * mm});
            skPoint(sketch, "E68.0.1.42", {"position": v(73.15, -38.8) * mm});
            skLineSegment(sketch, "E68.0.1.43", {"start": v(25.65, -36.8) * mm, "end": v(25.65, -8.3) * mm});
            skPoint(sketch, "E68.0.1.44", {"position": v(-73.15, -6.3) * mm});
            skPoint(sketch, "E68.0.1.45", {"position": v(23.75, -6.3) * mm});
            skLineSegment(sketch, "E68.0.1.46", {"start": v(27.65, -38.8) * mm, "end": v(46.45, -38.8) * mm});
            skLineSegment(sketch, "E68.0.1.47", {"start": v(0.95, -36.8) * mm, "end": v(0.95, -8.3) * mm});
            skLineSegment(sketch, "E68.0.1.48", {"start": v(73.15, -36.8) * mm, "end": v(73.15, -8.3) * mm});
            skPoint(sketch, "E68.0.1.49", {"position": v(48.45, -38.8) * mm});
            skPoint(sketch, "E68.0.1.50", {"position": v(-0.95, -6.3) * mm});
            skLineSegment(sketch, "E68.0.1.51", {"start": v(-71.15, -38.8) * mm, "end": v(-52.35, -38.8) * mm});
            skLineSegment(sketch, "E68.0.1.52", {"start": v(-50.35, -36.8) * mm, "end": v(-50.35, -8.3) * mm});
            skLineSegment(sketch, "E68.0.1.53", {"start": v(-21.75, -6.3) * mm, "end": v(-2.95, -6.3) * mm});
            skPoint(sketch, "E68.0.1.54", {"position": v(73.15, -6.3) * mm});
            skPoint(sketch, "E68.0.1.55", {"position": v(23.75, -38.8) * mm});
            skPoint(sketch, "E68.0.1.56", {"position": v(-48.45, -38.8) * mm});
            skPoint(sketch, "E68.0.1.57", {"position": v(-23.75, -6.3) * mm});
            skPoint(sketch, "E68.0.1.58", {"position": v(-97.85, -38.8) * mm});
            skPoint(sketch, "E68.0.1.59", {"position": v(75.05, -38.8) * mm});
            skPoint(sketch, "E68.0.1.60", {"position": v(-23.75, -38.8) * mm});
            skLineSegment(sketch, "E68.0.1.61", {"start": v(77.05, -38.8) * mm, "end": v(95.85, -38.8) * mm});
            skPoint(sketch, "E68.0.1.62", {"position": v(-23.75, -38.8) * mm});
            skPoint(sketch, "E68.0.1.63", {"position": v(25.65, -38.8) * mm});
            skPoint(sketch, "E68.0.1.64", {"position": v(0.95, -38.8) * mm});
            skPoint(sketch, "E68.0.1.65", {"position": v(-97.85, -38.8) * mm});
            skPoint(sketch, "E68.0.1.66", {"position": v(50.35, -38.8) * mm});
            skPoint(sketch, "E68.0.1.67", {"position": v(-48.45, -38.8) * mm});
            skPoint(sketch, "E68.0.1.68", {"position": v(75.05, -38.8) * mm});
            skPoint(sketch, "E68.0.1.69", {"position": v(-73.15, -38.8) * mm});
            skLineSegment(sketch, "E68.0.1.70", {"start": v(-97.85, -38.8) * mm, "end": v(-73.15, -38.8) * mm, "construction": true});
            skPoint(sketch, "E68.0.1.71", {"position": v(-75.05, -38.8) * mm});
            skLineSegment(sketch, "E68.0.1.72", {"start": v(-95.85, -38.8) * mm, "end": v(-77.05, -38.8) * mm});
            skArc(sketch, "E68.0.1.73", {"start": v(-95.85, -6.3) * mm, "mid": v(-97.26, -6.89) * mm, "end": v(-97.85, -8.3) * mm});
            skArc(sketch, "E68.0.1.74", {"start": v(77.05, -6.3) * mm, "mid": v(75.64, -6.89) * mm, "end": v(75.05, -8.3) * mm});
            skArc(sketch, "E68.0.1.75", {"start": v(95.85, -38.8) * mm, "mid": v(97.26, -38.21) * mm, "end": v(97.85, -36.8) * mm});
            skArc(sketch, "E68.0.1.76", {"start": v(-71.15, -6.3) * mm, "mid": v(-72.56, -6.89) * mm, "end": v(-73.15, -8.3) * mm});
            skArc(sketch, "E68.0.1.77", {"start": v(-75.05, -8.3) * mm, "mid": v(-75.64, -6.89) * mm, "end": v(-77.05, -6.3) * mm});
            skArc(sketch, "E68.0.1.78", {"start": v(73.15, -8.3) * mm, "mid": v(72.56, -6.89) * mm, "end": v(71.15, -6.3) * mm});
            skArc(sketch, "E68.0.1.79", {"start": v(-50.35, -8.3) * mm, "mid": v(-50.94, -6.89) * mm, "end": v(-52.35, -6.3) * mm});
            skArc(sketch, "E68.0.1.80", {"start": v(-46.45, -6.3) * mm, "mid": v(-47.86, -6.89) * mm, "end": v(-48.45, -8.3) * mm});
            skArc(sketch, "E68.0.1.81", {"start": v(97.85, -8.3) * mm, "mid": v(97.26, -6.89) * mm, "end": v(95.85, -6.3) * mm});
            skArc(sketch, "E68.0.1.82", {"start": v(23.75, -8.3) * mm, "mid": v(23.16, -6.89) * mm, "end": v(21.75, -6.3) * mm});
            skArc(sketch, "E68.0.1.83", {"start": v(48.45, -8.3) * mm, "mid": v(47.86, -6.89) * mm, "end": v(46.45, -6.3) * mm});
            skArc(sketch, "E68.0.1.84", {"start": v(27.65, -6.3) * mm, "mid": v(26.24, -6.89) * mm, "end": v(25.65, -8.3) * mm});
            skArc(sketch, "E68.0.1.85", {"start": v(52.35, -6.3) * mm, "mid": v(50.94, -6.89) * mm, "end": v(50.35, -8.3) * mm});
            skArc(sketch, "E68.0.1.86", {"start": v(-21.75, -6.3) * mm, "mid": v(-23.16, -6.89) * mm, "end": v(-23.75, -8.3) * mm});
            skArc(sketch, "E68.0.1.87", {"start": v(-0.95, -8.3) * mm, "mid": v(-1.54, -6.89) * mm, "end": v(-2.95, -6.3) * mm});
            skArc(sketch, "E68.0.1.88", {"start": v(-25.65, -8.3) * mm, "mid": v(-26.24, -6.89) * mm, "end": v(-27.65, -6.3) * mm});
            skArc(sketch, "E68.0.1.89", {"start": v(2.95, -6.3) * mm, "mid": v(1.54, -6.89) * mm, "end": v(0.95, -8.3) * mm});
            skArc(sketch, "E68.0.1.90", {"start": v(-77.05, -38.8) * mm, "mid": v(-75.64, -38.21) * mm, "end": v(-75.05, -36.8) * mm});
            skArc(sketch, "E68.0.1.91", {"start": v(50.35, -36.8) * mm, "mid": v(50.94, -38.21) * mm, "end": v(52.35, -38.8) * mm});
            skArc(sketch, "E68.0.1.92", {"start": v(-52.35, -38.8) * mm, "mid": v(-50.94, -38.21) * mm, "end": v(-50.35, -36.8) * mm});
            skArc(sketch, "E68.0.1.93", {"start": v(0.95, -36.8) * mm, "mid": v(1.54, -38.21) * mm, "end": v(2.95, -38.8) * mm});
            skArc(sketch, "E68.0.1.94", {"start": v(46.45, -38.8) * mm, "mid": v(47.86, -38.21) * mm, "end": v(48.45, -36.8) * mm});
            skArc(sketch, "E68.0.1.95", {"start": v(-73.15, -36.8) * mm, "mid": v(-72.56, -38.21) * mm, "end": v(-71.15, -38.8) * mm});
            skArc(sketch, "E68.0.1.96", {"start": v(-97.85, -36.8) * mm, "mid": v(-97.26, -38.21) * mm, "end": v(-95.85, -38.8) * mm});
            skArc(sketch, "E68.0.1.97", {"start": v(-48.45, -36.8) * mm, "mid": v(-47.86, -38.21) * mm, "end": v(-46.45, -38.8) * mm});
            skArc(sketch, "E68.0.1.98", {"start": v(-2.95, -38.8) * mm, "mid": v(-1.54, -38.21) * mm, "end": v(-0.95, -36.8) * mm});
            skArc(sketch, "E68.0.1.99", {"start": v(-48.45, -36.8) * mm, "mid": v(-47.86, -38.21) * mm, "end": v(-46.45, -38.8) * mm});
            skArc(sketch, "E68.0.1.100", {"start": v(-27.65, -38.8) * mm, "mid": v(-26.24, -38.21) * mm, "end": v(-25.65, -36.8) * mm});
            skArc(sketch, "E68.0.1.101", {"start": v(-23.75, -36.8) * mm, "mid": v(-23.16, -38.21) * mm, "end": v(-21.75, -38.8) * mm});
            skArc(sketch, "E68.0.1.102", {"start": v(0.95, -36.8) * mm, "mid": v(1.54, -38.21) * mm, "end": v(2.95, -38.8) * mm});
            skArc(sketch, "E68.0.1.103", {"start": v(50.35, -36.8) * mm, "mid": v(50.94, -38.21) * mm, "end": v(52.35, -38.8) * mm});
            skArc(sketch, "E68.0.1.104", {"start": v(-73.15, -36.8) * mm, "mid": v(-72.56, -38.21) * mm, "end": v(-71.15, -38.8) * mm});
            skArc(sketch, "E68.0.1.105", {"start": v(-97.85, -36.8) * mm, "mid": v(-97.26, -38.21) * mm, "end": v(-95.85, -38.8) * mm});
            skArc(sketch, "E68.0.1.106", {"start": v(-23.75, -36.8) * mm, "mid": v(-23.16, -38.21) * mm, "end": v(-21.75, -38.8) * mm});
            skArc(sketch, "E68.0.1.107", {"start": v(25.65, -36.8) * mm, "mid": v(26.24, -38.21) * mm, "end": v(27.65, -38.8) * mm});
            skArc(sketch, "E68.0.1.108", {"start": v(21.75, -38.8) * mm, "mid": v(23.16, -38.21) * mm, "end": v(23.75, -36.8) * mm});
            skArc(sketch, "E68.0.1.109", {"start": v(75.05, -36.8) * mm, "mid": v(75.64, -38.21) * mm, "end": v(77.05, -38.8) * mm});
            skArc(sketch, "E68.0.1.110", {"start": v(71.15, -38.8) * mm, "mid": v(72.56, -38.21) * mm, "end": v(73.15, -36.8) * mm});
            skArc(sketch, "E68.0.1.111", {"start": v(25.65, -36.8) * mm, "mid": v(26.24, -38.21) * mm, "end": v(27.65, -38.8) * mm});
            skArc(sketch, "E68.0.1.112", {"start": v(75.05, -36.8) * mm, "mid": v(75.64, -38.21) * mm, "end": v(77.05, -38.8) * mm});
            skLineSegment(sketch, "E68.0.2.0", {"start": v(-25.65, -1.6) * mm, "end": v(-25.65, 26.9) * mm});
            skPoint(sketch, "E68.0.2.1", {"position": v(25.65, -3.6) * mm});
            skLineSegment(sketch, "E68.0.2.2", {"start": v(-75.05, -1.6) * mm, "end": v(-75.05, 26.9) * mm});
            skPoint(sketch, "E68.0.2.3", {"position": v(75.05, 28.9) * mm});
            skPoint(sketch, "E68.0.2.4", {"position": v(-50.35, -3.6) * mm});
            skLineSegment(sketch, "E68.0.2.5", {"start": v(27.65, 28.9) * mm, "end": v(46.45, 28.9) * mm});
            skLineSegment(sketch, "E68.0.2.6", {"start": v(48.45, -1.6) * mm, "end": v(48.45, 26.9) * mm});
            skPoint(sketch, "E68.0.2.7", {"position": v(0.95, 28.9) * mm});
            skPoint(sketch, "E68.0.2.8", {"position": v(-73.15, -3.6) * mm});
            skLineSegment(sketch, "E68.0.2.9", {"start": v(-95.85, 28.9) * mm, "end": v(-77.05, 28.9) * mm});
            skLineSegment(sketch, "E68.0.2.10", {"start": v(-97.85, -1.6) * mm, "end": v(-97.85, 26.9) * mm});
            skLineSegment(sketch, "E68.0.2.11", {"start": v(75.05, -1.6) * mm, "end": v(75.05, 26.9) * mm});
            skLineSegment(sketch, "E68.0.2.12", {"start": v(-21.75, -3.6) * mm, "end": v(-2.95, -3.6) * mm});
            skPoint(sketch, "E68.0.2.13", {"position": v(50.35, 28.9) * mm});
            skPoint(sketch, "E68.0.2.14", {"position": v(97.85, 28.9) * mm});
            skPoint(sketch, "E68.0.2.15", {"position": v(-97.85, 28.9) * mm});
            skLineSegment(sketch, "E68.0.2.16", {"start": v(-23.75, -1.6) * mm, "end": v(-23.75, 26.9) * mm});
            skPoint(sketch, "E68.0.2.17", {"position": v(-0.95, -3.6) * mm});
            skPoint(sketch, "E68.0.2.18", {"position": v(-25.65, 28.9) * mm});
            skPoint(sketch, "E68.0.2.19", {"position": v(-25.65, -3.6) * mm});
            skLineSegment(sketch, "E68.0.2.20", {"start": v(-71.15, 28.9) * mm, "end": v(-52.35, 28.9) * mm});
            skPoint(sketch, "E68.0.2.21", {"position": v(97.85, -3.6) * mm});
            skPoint(sketch, "E68.0.2.22", {"position": v(-75.05, 28.9) * mm});
            skPoint(sketch, "E68.0.2.23", {"position": v(50.35, -3.6) * mm});
            skPoint(sketch, "E68.0.2.24", {"position": v(-48.45, 28.9) * mm});
            skLineSegment(sketch, "E68.0.2.25", {"start": v(2.95, 28.9) * mm, "end": v(21.75, 28.9) * mm});
            skPoint(sketch, "E68.0.2.26", {"position": v(-50.35, 28.9) * mm});
            skLineSegment(sketch, "E68.0.2.27", {"start": v(2.95, -3.6) * mm, "end": v(21.75, -3.6) * mm});
            skLineSegment(sketch, "E68.0.2.28", {"start": v(-73.15, -1.6) * mm, "end": v(-73.15, 26.9) * mm});
            skLineSegment(sketch, "E68.0.2.29", {"start": v(-46.45, 28.9) * mm, "end": v(-27.65, 28.9) * mm});
            skLineSegment(sketch, "E68.0.2.30", {"start": v(23.75, -1.6) * mm, "end": v(23.75, 26.9) * mm});
            skLineSegment(sketch, "E68.0.2.31", {"start": v(50.35, -1.6) * mm, "end": v(50.35, 26.9) * mm});
            skLineSegment(sketch, "E68.0.2.32", {"start": v(-46.45, -3.6) * mm, "end": v(-27.65, -3.6) * mm});
            skPoint(sketch, "E68.0.2.33", {"position": v(48.45, 28.9) * mm});
            skLineSegment(sketch, "E68.0.2.34", {"start": v(52.35, -3.6) * mm, "end": v(71.15, -3.6) * mm});
            skLineSegment(sketch, "E68.0.2.35", {"start": v(-0.95, -1.6) * mm, "end": v(-0.95, 26.9) * mm});
            skLineSegment(sketch, "E68.0.2.36", {"start": v(-48.45, -1.6) * mm, "end": v(-48.45, 26.9) * mm});
            skLineSegment(sketch, "E68.0.2.37", {"start": v(77.05, 28.9) * mm, "end": v(95.85, 28.9) * mm});
            skPoint(sketch, "E68.0.2.38", {"position": v(0.95, -3.6) * mm});
            skPoint(sketch, "E68.0.2.39", {"position": v(25.65, 28.9) * mm});
            skLineSegment(sketch, "E68.0.2.40", {"start": v(52.35, 28.9) * mm, "end": v(71.15, 28.9) * mm});
            skLineSegment(sketch, "E68.0.2.41", {"start": v(97.85, -1.6) * mm, "end": v(97.85, 26.9) * mm});
            skPoint(sketch, "E68.0.2.42", {"position": v(73.15, -3.6) * mm});
            skLineSegment(sketch, "E68.0.2.43", {"start": v(25.65, -1.6) * mm, "end": v(25.65, 26.9) * mm});
            skPoint(sketch, "E68.0.2.44", {"position": v(-73.15, 28.9) * mm});
            skPoint(sketch, "E68.0.2.45", {"position": v(23.75, 28.9) * mm});
            skLineSegment(sketch, "E68.0.2.46", {"start": v(27.65, -3.6) * mm, "end": v(46.45, -3.6) * mm});
            skLineSegment(sketch, "E68.0.2.47", {"start": v(0.95, -1.6) * mm, "end": v(0.95, 26.9) * mm});
            skLineSegment(sketch, "E68.0.2.48", {"start": v(73.15, -1.6) * mm, "end": v(73.15, 26.9) * mm});
            skPoint(sketch, "E68.0.2.49", {"position": v(48.45, -3.6) * mm});
            skPoint(sketch, "E68.0.2.50", {"position": v(-0.95, 28.9) * mm});
            skLineSegment(sketch, "E68.0.2.51", {"start": v(-71.15, -3.6) * mm, "end": v(-52.35, -3.6) * mm});
            skLineSegment(sketch, "E68.0.2.52", {"start": v(-50.35, -1.6) * mm, "end": v(-50.35, 26.9) * mm});
            skLineSegment(sketch, "E68.0.2.53", {"start": v(-21.75, 28.9) * mm, "end": v(-2.95, 28.9) * mm});
            skPoint(sketch, "E68.0.2.54", {"position": v(73.15, 28.9) * mm});
            skPoint(sketch, "E68.0.2.55", {"position": v(23.75, -3.6) * mm});
            skPoint(sketch, "E68.0.2.56", {"position": v(-48.45, -3.6) * mm});
            skPoint(sketch, "E68.0.2.57", {"position": v(-23.75, 28.9) * mm});
            skPoint(sketch, "E68.0.2.58", {"position": v(-97.85, -3.6) * mm});
            skPoint(sketch, "E68.0.2.59", {"position": v(75.05, -3.6) * mm});
            skPoint(sketch, "E68.0.2.60", {"position": v(-23.75, -3.6) * mm});
            skLineSegment(sketch, "E68.0.2.61", {"start": v(77.05, -3.6) * mm, "end": v(95.85, -3.6) * mm});
            skPoint(sketch, "E68.0.2.62", {"position": v(-23.75, -3.6) * mm});
            skPoint(sketch, "E68.0.2.63", {"position": v(25.65, -3.6) * mm});
            skPoint(sketch, "E68.0.2.64", {"position": v(0.95, -3.6) * mm});
            skPoint(sketch, "E68.0.2.65", {"position": v(-97.85, -3.6) * mm});
            skPoint(sketch, "E68.0.2.66", {"position": v(50.35, -3.6) * mm});
            skPoint(sketch, "E68.0.2.67", {"position": v(-48.45, -3.6) * mm});
            skPoint(sketch, "E68.0.2.68", {"position": v(75.05, -3.6) * mm});
            skPoint(sketch, "E68.0.2.69", {"position": v(-73.15, -3.6) * mm});
            skLineSegment(sketch, "E68.0.2.70", {"start": v(-97.85, -3.6) * mm, "end": v(-73.15, -3.6) * mm, "construction": true});
            skPoint(sketch, "E68.0.2.71", {"position": v(-75.05, -3.6) * mm});
            skLineSegment(sketch, "E68.0.2.72", {"start": v(-95.85, -3.6) * mm, "end": v(-77.05, -3.6) * mm});
            skArc(sketch, "E68.0.2.73", {"start": v(-95.85, 28.9) * mm, "mid": v(-97.26, 28.31) * mm, "end": v(-97.85, 26.9) * mm});
            skArc(sketch, "E68.0.2.74", {"start": v(77.05, 28.9) * mm, "mid": v(75.64, 28.31) * mm, "end": v(75.05, 26.9) * mm});
            skArc(sketch, "E68.0.2.75", {"start": v(95.85, -3.6) * mm, "mid": v(97.26, -3.01) * mm, "end": v(97.85, -1.6) * mm});
            skArc(sketch, "E68.0.2.76", {"start": v(-71.15, 28.9) * mm, "mid": v(-72.56, 28.31) * mm, "end": v(-73.15, 26.9) * mm});
            skArc(sketch, "E68.0.2.77", {"start": v(-75.05, 26.9) * mm, "mid": v(-75.64, 28.31) * mm, "end": v(-77.05, 28.9) * mm});
            skArc(sketch, "E68.0.2.78", {"start": v(73.15, 26.9) * mm, "mid": v(72.56, 28.31) * mm, "end": v(71.15, 28.9) * mm});
            skArc(sketch, "E68.0.2.79", {"start": v(-50.35, 26.9) * mm, "mid": v(-50.94, 28.31) * mm, "end": v(-52.35, 28.9) * mm});
            skArc(sketch, "E68.0.2.80", {"start": v(-46.45, 28.9) * mm, "mid": v(-47.86, 28.31) * mm, "end": v(-48.45, 26.9) * mm});
            skArc(sketch, "E68.0.2.81", {"start": v(97.85, 26.9) * mm, "mid": v(97.26, 28.31) * mm, "end": v(95.85, 28.9) * mm});
            skArc(sketch, "E68.0.2.82", {"start": v(23.75, 26.9) * mm, "mid": v(23.16, 28.31) * mm, "end": v(21.75, 28.9) * mm});
            skArc(sketch, "E68.0.2.83", {"start": v(48.45, 26.9) * mm, "mid": v(47.86, 28.31) * mm, "end": v(46.45, 28.9) * mm});
            skArc(sketch, "E68.0.2.84", {"start": v(27.65, 28.9) * mm, "mid": v(26.24, 28.31) * mm, "end": v(25.65, 26.9) * mm});
            skArc(sketch, "E68.0.2.85", {"start": v(52.35, 28.9) * mm, "mid": v(50.94, 28.31) * mm, "end": v(50.35, 26.9) * mm});
            skArc(sketch, "E68.0.2.86", {"start": v(-21.75, 28.9) * mm, "mid": v(-23.16, 28.31) * mm, "end": v(-23.75, 26.9) * mm});
            skArc(sketch, "E68.0.2.87", {"start": v(-0.95, 26.9) * mm, "mid": v(-1.54, 28.31) * mm, "end": v(-2.95, 28.9) * mm});
            skArc(sketch, "E68.0.2.88", {"start": v(-25.65, 26.9) * mm, "mid": v(-26.24, 28.31) * mm, "end": v(-27.65, 28.9) * mm});
            skArc(sketch, "E68.0.2.89", {"start": v(2.95, 28.9) * mm, "mid": v(1.54, 28.31) * mm, "end": v(0.95, 26.9) * mm});
            skArc(sketch, "E68.0.2.90", {"start": v(-77.05, -3.6) * mm, "mid": v(-75.64, -3.01) * mm, "end": v(-75.05, -1.6) * mm});
            skArc(sketch, "E68.0.2.91", {"start": v(50.35, -1.6) * mm, "mid": v(50.94, -3.01) * mm, "end": v(52.35, -3.6) * mm});
            skArc(sketch, "E68.0.2.92", {"start": v(-52.35, -3.6) * mm, "mid": v(-50.94, -3.01) * mm, "end": v(-50.35, -1.6) * mm});
            skArc(sketch, "E68.0.2.93", {"start": v(0.95, -1.6) * mm, "mid": v(1.54, -3.01) * mm, "end": v(2.95, -3.6) * mm});
            skArc(sketch, "E68.0.2.94", {"start": v(46.45, -3.6) * mm, "mid": v(47.86, -3.01) * mm, "end": v(48.45, -1.6) * mm});
            skArc(sketch, "E68.0.2.95", {"start": v(-73.15, -1.6) * mm, "mid": v(-72.56, -3.01) * mm, "end": v(-71.15, -3.6) * mm});
            skArc(sketch, "E68.0.2.96", {"start": v(-97.85, -1.6) * mm, "mid": v(-97.26, -3.01) * mm, "end": v(-95.85, -3.6) * mm});
            skArc(sketch, "E68.0.2.97", {"start": v(-48.45, -1.6) * mm, "mid": v(-47.86, -3.01) * mm, "end": v(-46.45, -3.6) * mm});
            skArc(sketch, "E68.0.2.98", {"start": v(-2.95, -3.6) * mm, "mid": v(-1.54, -3.01) * mm, "end": v(-0.95, -1.6) * mm});
            skArc(sketch, "E68.0.2.99", {"start": v(-48.45, -1.6) * mm, "mid": v(-47.86, -3.01) * mm, "end": v(-46.45, -3.6) * mm});
            skArc(sketch, "E68.0.2.100", {"start": v(-27.65, -3.6) * mm, "mid": v(-26.24, -3.01) * mm, "end": v(-25.65, -1.6) * mm});
            skArc(sketch, "E68.0.2.101", {"start": v(-23.75, -1.6) * mm, "mid": v(-23.16, -3.01) * mm, "end": v(-21.75, -3.6) * mm});
            skArc(sketch, "E68.0.2.102", {"start": v(0.95, -1.6) * mm, "mid": v(1.54, -3.01) * mm, "end": v(2.95, -3.6) * mm});
            skArc(sketch, "E68.0.2.103", {"start": v(50.35, -1.6) * mm, "mid": v(50.94, -3.01) * mm, "end": v(52.35, -3.6) * mm});
            skArc(sketch, "E68.0.2.104", {"start": v(-73.15, -1.6) * mm, "mid": v(-72.56, -3.01) * mm, "end": v(-71.15, -3.6) * mm});
            skArc(sketch, "E68.0.2.105", {"start": v(-97.85, -1.6) * mm, "mid": v(-97.26, -3.01) * mm, "end": v(-95.85, -3.6) * mm});
            skArc(sketch, "E68.0.2.106", {"start": v(-23.75, -1.6) * mm, "mid": v(-23.16, -3.01) * mm, "end": v(-21.75, -3.6) * mm});
            skArc(sketch, "E68.0.2.107", {"start": v(25.65, -1.6) * mm, "mid": v(26.24, -3.01) * mm, "end": v(27.65, -3.6) * mm});
            skArc(sketch, "E68.0.2.108", {"start": v(21.75, -3.6) * mm, "mid": v(23.16, -3.01) * mm, "end": v(23.75, -1.6) * mm});
            skArc(sketch, "E68.0.2.109", {"start": v(75.05, -1.6) * mm, "mid": v(75.64, -3.01) * mm, "end": v(77.05, -3.6) * mm});
            skArc(sketch, "E68.0.2.110", {"start": v(71.15, -3.6) * mm, "mid": v(72.56, -3.01) * mm, "end": v(73.15, -1.6) * mm});
            skArc(sketch, "E68.0.2.111", {"start": v(25.65, -1.6) * mm, "mid": v(26.24, -3.01) * mm, "end": v(27.65, -3.6) * mm});
            skArc(sketch, "E68.0.2.112", {"start": v(75.05, -1.6) * mm, "mid": v(75.64, -3.01) * mm, "end": v(77.05, -3.6) * mm});
            skLineSegment(sketch, "E68.0.3.0", {"start": v(-25.65, 33.6) * mm, "end": v(-25.65, 62.1) * mm});
            skPoint(sketch, "E68.0.3.1", {"position": v(25.65, 31.6) * mm});
            skLineSegment(sketch, "E68.0.3.2", {"start": v(-75.05, 33.6) * mm, "end": v(-75.05, 62.1) * mm});
            skPoint(sketch, "E68.0.3.3", {"position": v(75.05, 64.1) * mm});
            skPoint(sketch, "E68.0.3.4", {"position": v(-50.35, 31.6) * mm});
            skLineSegment(sketch, "E68.0.3.5", {"start": v(27.65, 64.1) * mm, "end": v(46.45, 64.1) * mm});
            skLineSegment(sketch, "E68.0.3.6", {"start": v(48.45, 33.6) * mm, "end": v(48.45, 62.1) * mm});
            skPoint(sketch, "E68.0.3.7", {"position": v(0.95, 64.1) * mm});
            skPoint(sketch, "E68.0.3.8", {"position": v(-73.15, 31.6) * mm});
            skLineSegment(sketch, "E68.0.3.9", {"start": v(-95.85, 64.1) * mm, "end": v(-77.05, 64.1) * mm});
            skLineSegment(sketch, "E68.0.3.10", {"start": v(-97.85, 33.6) * mm, "end": v(-97.85, 62.1) * mm});
            skLineSegment(sketch, "E68.0.3.11", {"start": v(75.05, 33.6) * mm, "end": v(75.05, 62.1) * mm});
            skLineSegment(sketch, "E68.0.3.12", {"start": v(-21.75, 31.6) * mm, "end": v(-2.95, 31.6) * mm});
            skPoint(sketch, "E68.0.3.13", {"position": v(50.35, 64.1) * mm});
            skPoint(sketch, "E68.0.3.14", {"position": v(97.85, 64.1) * mm});
            skPoint(sketch, "E68.0.3.15", {"position": v(-97.85, 64.1) * mm});
            skLineSegment(sketch, "E68.0.3.16", {"start": v(-23.75, 33.6) * mm, "end": v(-23.75, 62.1) * mm});
            skPoint(sketch, "E68.0.3.17", {"position": v(-0.95, 31.6) * mm});
            skPoint(sketch, "E68.0.3.18", {"position": v(-25.65, 64.1) * mm});
            skPoint(sketch, "E68.0.3.19", {"position": v(-25.65, 31.6) * mm});
            skLineSegment(sketch, "E68.0.3.20", {"start": v(-71.15, 64.1) * mm, "end": v(-52.35, 64.1) * mm});
            skPoint(sketch, "E68.0.3.21", {"position": v(97.85, 31.6) * mm});
            skPoint(sketch, "E68.0.3.22", {"position": v(-75.05, 64.1) * mm});
            skPoint(sketch, "E68.0.3.23", {"position": v(50.35, 31.6) * mm});
            skPoint(sketch, "E68.0.3.24", {"position": v(-48.45, 64.1) * mm});
            skLineSegment(sketch, "E68.0.3.25", {"start": v(2.95, 64.1) * mm, "end": v(21.75, 64.1) * mm});
            skPoint(sketch, "E68.0.3.26", {"position": v(-50.35, 64.1) * mm});
            skLineSegment(sketch, "E68.0.3.27", {"start": v(2.95, 31.6) * mm, "end": v(21.75, 31.6) * mm});
            skLineSegment(sketch, "E68.0.3.28", {"start": v(-73.15, 33.6) * mm, "end": v(-73.15, 62.1) * mm});
            skLineSegment(sketch, "E68.0.3.29", {"start": v(-46.45, 64.1) * mm, "end": v(-27.65, 64.1) * mm});
            skLineSegment(sketch, "E68.0.3.30", {"start": v(23.75, 33.6) * mm, "end": v(23.75, 62.1) * mm});
            skLineSegment(sketch, "E68.0.3.31", {"start": v(50.35, 33.6) * mm, "end": v(50.35, 62.1) * mm});
            skLineSegment(sketch, "E68.0.3.32", {"start": v(-46.45, 31.6) * mm, "end": v(-27.65, 31.6) * mm});
            skPoint(sketch, "E68.0.3.33", {"position": v(48.45, 64.1) * mm});
            skLineSegment(sketch, "E68.0.3.34", {"start": v(52.35, 31.6) * mm, "end": v(71.15, 31.6) * mm});
            skLineSegment(sketch, "E68.0.3.35", {"start": v(-0.95, 33.6) * mm, "end": v(-0.95, 62.1) * mm});
            skLineSegment(sketch, "E68.0.3.36", {"start": v(-48.45, 33.6) * mm, "end": v(-48.45, 62.1) * mm});
            skLineSegment(sketch, "E68.0.3.37", {"start": v(77.05, 64.1) * mm, "end": v(95.85, 64.1) * mm});
            skPoint(sketch, "E68.0.3.38", {"position": v(0.95, 31.6) * mm});
            skPoint(sketch, "E68.0.3.39", {"position": v(25.65, 64.1) * mm});
            skLineSegment(sketch, "E68.0.3.40", {"start": v(52.35, 64.1) * mm, "end": v(71.15, 64.1) * mm});
            skLineSegment(sketch, "E68.0.3.41", {"start": v(97.85, 33.6) * mm, "end": v(97.85, 62.1) * mm});
            skPoint(sketch, "E68.0.3.42", {"position": v(73.15, 31.6) * mm});
            skLineSegment(sketch, "E68.0.3.43", {"start": v(25.65, 33.6) * mm, "end": v(25.65, 62.1) * mm});
            skPoint(sketch, "E68.0.3.44", {"position": v(-73.15, 64.1) * mm});
            skPoint(sketch, "E68.0.3.45", {"position": v(23.75, 64.1) * mm});
            skLineSegment(sketch, "E68.0.3.46", {"start": v(27.65, 31.6) * mm, "end": v(46.45, 31.6) * mm});
            skLineSegment(sketch, "E68.0.3.47", {"start": v(0.95, 33.6) * mm, "end": v(0.95, 62.1) * mm});
            skLineSegment(sketch, "E68.0.3.48", {"start": v(73.15, 33.6) * mm, "end": v(73.15, 62.1) * mm});
            skPoint(sketch, "E68.0.3.49", {"position": v(48.45, 31.6) * mm});
            skPoint(sketch, "E68.0.3.50", {"position": v(-0.95, 64.1) * mm});
            skLineSegment(sketch, "E68.0.3.51", {"start": v(-71.15, 31.6) * mm, "end": v(-52.35, 31.6) * mm});
            skLineSegment(sketch, "E68.0.3.52", {"start": v(-50.35, 33.6) * mm, "end": v(-50.35, 62.1) * mm});
            skLineSegment(sketch, "E68.0.3.53", {"start": v(-21.75, 64.1) * mm, "end": v(-2.95, 64.1) * mm});
            skPoint(sketch, "E68.0.3.54", {"position": v(73.15, 64.1) * mm});
            skPoint(sketch, "E68.0.3.55", {"position": v(23.75, 31.6) * mm});
            skPoint(sketch, "E68.0.3.56", {"position": v(-48.45, 31.6) * mm});
            skPoint(sketch, "E68.0.3.57", {"position": v(-23.75, 64.1) * mm});
            skPoint(sketch, "E68.0.3.58", {"position": v(-97.85, 31.6) * mm});
            skPoint(sketch, "E68.0.3.59", {"position": v(75.05, 31.6) * mm});
            skPoint(sketch, "E68.0.3.60", {"position": v(-23.75, 31.6) * mm});
            skLineSegment(sketch, "E68.0.3.61", {"start": v(77.05, 31.6) * mm, "end": v(95.85, 31.6) * mm});
            skPoint(sketch, "E68.0.3.62", {"position": v(-23.75, 31.6) * mm});
            skPoint(sketch, "E68.0.3.63", {"position": v(25.65, 31.6) * mm});
            skPoint(sketch, "E68.0.3.64", {"position": v(0.95, 31.6) * mm});
            skPoint(sketch, "E68.0.3.65", {"position": v(-97.85, 31.6) * mm});
            skPoint(sketch, "E68.0.3.66", {"position": v(50.35, 31.6) * mm});
            skPoint(sketch, "E68.0.3.67", {"position": v(-48.45, 31.6) * mm});
            skPoint(sketch, "E68.0.3.68", {"position": v(75.05, 31.6) * mm});
            skPoint(sketch, "E68.0.3.69", {"position": v(-73.15, 31.6) * mm});
            skLineSegment(sketch, "E68.0.3.70", {"start": v(-97.85, 31.6) * mm, "end": v(-73.15, 31.6) * mm, "construction": true});
            skPoint(sketch, "E68.0.3.71", {"position": v(-75.05, 31.6) * mm});
            skLineSegment(sketch, "E68.0.3.72", {"start": v(-95.85, 31.6) * mm, "end": v(-77.05, 31.6) * mm});
            skArc(sketch, "E68.0.3.73", {"start": v(-95.85, 64.1) * mm, "mid": v(-97.26, 63.51) * mm, "end": v(-97.85, 62.1) * mm});
            skArc(sketch, "E68.0.3.74", {"start": v(77.05, 64.1) * mm, "mid": v(75.64, 63.51) * mm, "end": v(75.05, 62.1) * mm});
            skArc(sketch, "E68.0.3.75", {"start": v(95.85, 31.6) * mm, "mid": v(97.26, 32.19) * mm, "end": v(97.85, 33.6) * mm});
            skArc(sketch, "E68.0.3.76", {"start": v(-71.15, 64.1) * mm, "mid": v(-72.56, 63.51) * mm, "end": v(-73.15, 62.1) * mm});
            skArc(sketch, "E68.0.3.77", {"start": v(-75.05, 62.1) * mm, "mid": v(-75.64, 63.51) * mm, "end": v(-77.05, 64.1) * mm});
            skArc(sketch, "E68.0.3.78", {"start": v(73.15, 62.1) * mm, "mid": v(72.56, 63.51) * mm, "end": v(71.15, 64.1) * mm});
            skArc(sketch, "E68.0.3.79", {"start": v(-50.35, 62.1) * mm, "mid": v(-50.94, 63.51) * mm, "end": v(-52.35, 64.1) * mm});
            skArc(sketch, "E68.0.3.80", {"start": v(-46.45, 64.1) * mm, "mid": v(-47.86, 63.51) * mm, "end": v(-48.45, 62.1) * mm});
            skArc(sketch, "E68.0.3.81", {"start": v(97.85, 62.1) * mm, "mid": v(97.26, 63.51) * mm, "end": v(95.85, 64.1) * mm});
            skArc(sketch, "E68.0.3.82", {"start": v(23.75, 62.1) * mm, "mid": v(23.16, 63.51) * mm, "end": v(21.75, 64.1) * mm});
            skArc(sketch, "E68.0.3.83", {"start": v(48.45, 62.1) * mm, "mid": v(47.86, 63.51) * mm, "end": v(46.45, 64.1) * mm});
            skArc(sketch, "E68.0.3.84", {"start": v(27.65, 64.1) * mm, "mid": v(26.24, 63.51) * mm, "end": v(25.65, 62.1) * mm});
            skArc(sketch, "E68.0.3.85", {"start": v(52.35, 64.1) * mm, "mid": v(50.94, 63.51) * mm, "end": v(50.35, 62.1) * mm});
            skArc(sketch, "E68.0.3.86", {"start": v(-21.75, 64.1) * mm, "mid": v(-23.16, 63.51) * mm, "end": v(-23.75, 62.1) * mm});
            skArc(sketch, "E68.0.3.87", {"start": v(-0.95, 62.1) * mm, "mid": v(-1.54, 63.51) * mm, "end": v(-2.95, 64.1) * mm});
            skArc(sketch, "E68.0.3.88", {"start": v(-25.65, 62.1) * mm, "mid": v(-26.24, 63.51) * mm, "end": v(-27.65, 64.1) * mm});
            skArc(sketch, "E68.0.3.89", {"start": v(2.95, 64.1) * mm, "mid": v(1.54, 63.51) * mm, "end": v(0.95, 62.1) * mm});
            skArc(sketch, "E68.0.3.90", {"start": v(-77.05, 31.6) * mm, "mid": v(-75.64, 32.19) * mm, "end": v(-75.05, 33.6) * mm});
            skArc(sketch, "E68.0.3.91", {"start": v(50.35, 33.6) * mm, "mid": v(50.94, 32.19) * mm, "end": v(52.35, 31.6) * mm});
            skArc(sketch, "E68.0.3.92", {"start": v(-52.35, 31.6) * mm, "mid": v(-50.94, 32.19) * mm, "end": v(-50.35, 33.6) * mm});
            skArc(sketch, "E68.0.3.93", {"start": v(0.95, 33.6) * mm, "mid": v(1.54, 32.19) * mm, "end": v(2.95, 31.6) * mm});
            skArc(sketch, "E68.0.3.94", {"start": v(46.45, 31.6) * mm, "mid": v(47.86, 32.19) * mm, "end": v(48.45, 33.6) * mm});
            skArc(sketch, "E68.0.3.95", {"start": v(-73.15, 33.6) * mm, "mid": v(-72.56, 32.19) * mm, "end": v(-71.15, 31.6) * mm});
            skArc(sketch, "E68.0.3.96", {"start": v(-97.85, 33.6) * mm, "mid": v(-97.26, 32.19) * mm, "end": v(-95.85, 31.6) * mm});
            skArc(sketch, "E68.0.3.97", {"start": v(-48.45, 33.6) * mm, "mid": v(-47.86, 32.19) * mm, "end": v(-46.45, 31.6) * mm});
            skArc(sketch, "E68.0.3.98", {"start": v(-2.95, 31.6) * mm, "mid": v(-1.54, 32.19) * mm, "end": v(-0.95, 33.6) * mm});
            skArc(sketch, "E68.0.3.99", {"start": v(-48.45, 33.6) * mm, "mid": v(-47.86, 32.19) * mm, "end": v(-46.45, 31.6) * mm});
            skArc(sketch, "E68.0.3.100", {"start": v(-27.65, 31.6) * mm, "mid": v(-26.24, 32.19) * mm, "end": v(-25.65, 33.6) * mm});
            skArc(sketch, "E68.0.3.101", {"start": v(-23.75, 33.6) * mm, "mid": v(-23.16, 32.19) * mm, "end": v(-21.75, 31.6) * mm});
            skArc(sketch, "E68.0.3.102", {"start": v(0.95, 33.6) * mm, "mid": v(1.54, 32.19) * mm, "end": v(2.95, 31.6) * mm});
            skArc(sketch, "E68.0.3.103", {"start": v(50.35, 33.6) * mm, "mid": v(50.94, 32.19) * mm, "end": v(52.35, 31.6) * mm});
            skArc(sketch, "E68.0.3.104", {"start": v(-73.15, 33.6) * mm, "mid": v(-72.56, 32.19) * mm, "end": v(-71.15, 31.6) * mm});
            skArc(sketch, "E68.0.3.105", {"start": v(-97.85, 33.6) * mm, "mid": v(-97.26, 32.19) * mm, "end": v(-95.85, 31.6) * mm});
            skArc(sketch, "E68.0.3.106", {"start": v(-23.75, 33.6) * mm, "mid": v(-23.16, 32.19) * mm, "end": v(-21.75, 31.6) * mm});
            skArc(sketch, "E68.0.3.107", {"start": v(25.65, 33.6) * mm, "mid": v(26.24, 32.19) * mm, "end": v(27.65, 31.6) * mm});
            skArc(sketch, "E68.0.3.108", {"start": v(21.75, 31.6) * mm, "mid": v(23.16, 32.19) * mm, "end": v(23.75, 33.6) * mm});
            skArc(sketch, "E68.0.3.109", {"start": v(75.05, 33.6) * mm, "mid": v(75.64, 32.19) * mm, "end": v(77.05, 31.6) * mm});
            skArc(sketch, "E68.0.3.110", {"start": v(71.15, 31.6) * mm, "mid": v(72.56, 32.19) * mm, "end": v(73.15, 33.6) * mm});
            skArc(sketch, "E68.0.3.111", {"start": v(25.65, 33.6) * mm, "mid": v(26.24, 32.19) * mm, "end": v(27.65, 31.6) * mm});
            skArc(sketch, "E68.0.3.112", {"start": v(75.05, 33.6) * mm, "mid": v(75.64, 32.19) * mm, "end": v(77.05, 31.6) * mm});
            skLineSegment(sketch, "E68.1.1.0", {"start": v(-25.65, -36.8) * mm, "end": v(-25.65, -8.3) * mm});
            skPoint(sketch, "E68.1.1.1", {"position": v(25.65, -38.8) * mm});
            skLineSegment(sketch, "E68.1.1.2", {"start": v(-75.05, -36.8) * mm, "end": v(-75.05, -8.3) * mm});
            skPoint(sketch, "E68.1.1.3", {"position": v(75.05, -6.3) * mm});
            skPoint(sketch, "E68.1.1.4", {"position": v(-50.35, -38.8) * mm});
            skLineSegment(sketch, "E68.1.1.5", {"start": v(27.65, -6.3) * mm, "end": v(46.45, -6.3) * mm});
            skLineSegment(sketch, "E68.1.1.6", {"start": v(48.45, -36.8) * mm, "end": v(48.45, -8.3) * mm});
            skPoint(sketch, "E68.1.1.7", {"position": v(0.95, -6.3) * mm});
            skPoint(sketch, "E68.1.1.8", {"position": v(-73.15, -38.8) * mm});
            skLineSegment(sketch, "E68.1.1.9", {"start": v(-95.85, -6.3) * mm, "end": v(-77.05, -6.3) * mm});
            skLineSegment(sketch, "E68.1.1.10", {"start": v(-97.85, -36.8) * mm, "end": v(-97.85, -8.3) * mm});
            skLineSegment(sketch, "E68.1.1.11", {"start": v(75.05, -36.8) * mm, "end": v(75.05, -8.3) * mm});
            skLineSegment(sketch, "E68.1.1.12", {"start": v(-21.75, -38.8) * mm, "end": v(-2.95, -38.8) * mm});
            skPoint(sketch, "E68.1.1.13", {"position": v(50.35, -6.3) * mm});
            skPoint(sketch, "E68.1.1.14", {"position": v(97.85, -6.3) * mm});
            skPoint(sketch, "E68.1.1.15", {"position": v(-97.85, -6.3) * mm});
            skLineSegment(sketch, "E68.1.1.16", {"start": v(-23.75, -36.8) * mm, "end": v(-23.75, -8.3) * mm});
            skPoint(sketch, "E68.1.1.17", {"position": v(-0.95, -38.8) * mm});
            skPoint(sketch, "E68.1.1.18", {"position": v(-25.65, -6.3) * mm});
            skPoint(sketch, "E68.1.1.19", {"position": v(-25.65, -38.8) * mm});
            skLineSegment(sketch, "E68.1.1.20", {"start": v(-71.15, -6.3) * mm, "end": v(-52.35, -6.3) * mm});
            skPoint(sketch, "E68.1.1.21", {"position": v(97.85, -38.8) * mm});
            skPoint(sketch, "E68.1.1.22", {"position": v(-75.05, -6.3) * mm});
            skPoint(sketch, "E68.1.1.23", {"position": v(50.35, -38.8) * mm});
            skPoint(sketch, "E68.1.1.24", {"position": v(-48.45, -6.3) * mm});
            skLineSegment(sketch, "E68.1.1.25", {"start": v(2.95, -6.3) * mm, "end": v(21.75, -6.3) * mm});
            skPoint(sketch, "E68.1.1.26", {"position": v(-50.35, -6.3) * mm});
            skLineSegment(sketch, "E68.1.1.27", {"start": v(2.95, -38.8) * mm, "end": v(21.75, -38.8) * mm});
            skLineSegment(sketch, "E68.1.1.28", {"start": v(-73.15, -36.8) * mm, "end": v(-73.15, -8.3) * mm});
            skLineSegment(sketch, "E68.1.1.29", {"start": v(-46.45, -6.3) * mm, "end": v(-27.65, -6.3) * mm});
            skLineSegment(sketch, "E68.1.1.30", {"start": v(23.75, -36.8) * mm, "end": v(23.75, -8.3) * mm});
            skLineSegment(sketch, "E68.1.1.31", {"start": v(50.35, -36.8) * mm, "end": v(50.35, -8.3) * mm});
            skLineSegment(sketch, "E68.1.1.32", {"start": v(-46.45, -38.8) * mm, "end": v(-27.65, -38.8) * mm});
            skPoint(sketch, "E68.1.1.33", {"position": v(48.45, -6.3) * mm});
            skLineSegment(sketch, "E68.1.1.34", {"start": v(52.35, -38.8) * mm, "end": v(71.15, -38.8) * mm});
            skLineSegment(sketch, "E68.1.1.35", {"start": v(-0.95, -36.8) * mm, "end": v(-0.95, -8.3) * mm});
            skLineSegment(sketch, "E68.1.1.36", {"start": v(-48.45, -36.8) * mm, "end": v(-48.45, -8.3) * mm});
            skLineSegment(sketch, "E68.1.1.37", {"start": v(77.05, -6.3) * mm, "end": v(95.85, -6.3) * mm});
            skPoint(sketch, "E68.1.1.38", {"position": v(0.95, -38.8) * mm});
            skPoint(sketch, "E68.1.1.39", {"position": v(25.65, -6.3) * mm});
            skLineSegment(sketch, "E68.1.1.40", {"start": v(52.35, -6.3) * mm, "end": v(71.15, -6.3) * mm});
            skLineSegment(sketch, "E68.1.1.41", {"start": v(97.85, -36.8) * mm, "end": v(97.85, -8.3) * mm});
            skPoint(sketch, "E68.1.1.42", {"position": v(73.15, -38.8) * mm});
            skLineSegment(sketch, "E68.1.1.43", {"start": v(25.65, -36.8) * mm, "end": v(25.65, -8.3) * mm});
            skPoint(sketch, "E68.1.1.44", {"position": v(-73.15, -6.3) * mm});
            skPoint(sketch, "E68.1.1.45", {"position": v(23.75, -6.3) * mm});
            skLineSegment(sketch, "E68.1.1.46", {"start": v(27.65, -38.8) * mm, "end": v(46.45, -38.8) * mm});
            skLineSegment(sketch, "E68.1.1.47", {"start": v(0.95, -36.8) * mm, "end": v(0.95, -8.3) * mm});
            skLineSegment(sketch, "E68.1.1.48", {"start": v(73.15, -36.8) * mm, "end": v(73.15, -8.3) * mm});
            skPoint(sketch, "E68.1.1.49", {"position": v(48.45, -38.8) * mm});
            skPoint(sketch, "E68.1.1.50", {"position": v(-0.95, -6.3) * mm});
            skLineSegment(sketch, "E68.1.1.51", {"start": v(-71.15, -38.8) * mm, "end": v(-52.35, -38.8) * mm});
            skLineSegment(sketch, "E68.1.1.52", {"start": v(-50.35, -36.8) * mm, "end": v(-50.35, -8.3) * mm});
            skLineSegment(sketch, "E68.1.1.53", {"start": v(-21.75, -6.3) * mm, "end": v(-2.95, -6.3) * mm});
            skPoint(sketch, "E68.1.1.54", {"position": v(73.15, -6.3) * mm});
            skPoint(sketch, "E68.1.1.55", {"position": v(23.75, -38.8) * mm});
            skPoint(sketch, "E68.1.1.56", {"position": v(-48.45, -38.8) * mm});
            skPoint(sketch, "E68.1.1.57", {"position": v(-23.75, -6.3) * mm});
            skPoint(sketch, "E68.1.1.58", {"position": v(-97.85, -38.8) * mm});
            skPoint(sketch, "E68.1.1.59", {"position": v(75.05, -38.8) * mm});
            skPoint(sketch, "E68.1.1.60", {"position": v(-23.75, -38.8) * mm});
            skLineSegment(sketch, "E68.1.1.61", {"start": v(77.05, -38.8) * mm, "end": v(95.85, -38.8) * mm});
            skPoint(sketch, "E68.1.1.62", {"position": v(-23.75, -38.8) * mm});
            skPoint(sketch, "E68.1.1.63", {"position": v(25.65, -38.8) * mm});
            skPoint(sketch, "E68.1.1.64", {"position": v(0.95, -38.8) * mm});
            skPoint(sketch, "E68.1.1.65", {"position": v(-97.85, -38.8) * mm});
            skPoint(sketch, "E68.1.1.66", {"position": v(50.35, -38.8) * mm});
            skPoint(sketch, "E68.1.1.67", {"position": v(-48.45, -38.8) * mm});
            skPoint(sketch, "E68.1.1.68", {"position": v(75.05, -38.8) * mm});
            skPoint(sketch, "E68.1.1.69", {"position": v(-73.15, -38.8) * mm});
            skLineSegment(sketch, "E68.1.1.70", {"start": v(-97.85, -38.8) * mm, "end": v(-73.15, -38.8) * mm, "construction": true});
            skPoint(sketch, "E68.1.1.71", {"position": v(-75.05, -38.8) * mm});
            skLineSegment(sketch, "E68.1.1.72", {"start": v(-95.85, -38.8) * mm, "end": v(-77.05, -38.8) * mm});
            skArc(sketch, "E68.1.1.73", {"start": v(-95.85, -6.3) * mm, "mid": v(-97.26, -6.89) * mm, "end": v(-97.85, -8.3) * mm});
            skArc(sketch, "E68.1.1.74", {"start": v(77.05, -6.3) * mm, "mid": v(75.64, -6.89) * mm, "end": v(75.05, -8.3) * mm});
            skArc(sketch, "E68.1.1.75", {"start": v(95.85, -38.8) * mm, "mid": v(97.26, -38.21) * mm, "end": v(97.85, -36.8) * mm});
            skArc(sketch, "E68.1.1.76", {"start": v(-71.15, -6.3) * mm, "mid": v(-72.56, -6.89) * mm, "end": v(-73.15, -8.3) * mm});
            skArc(sketch, "E68.1.1.77", {"start": v(-75.05, -8.3) * mm, "mid": v(-75.64, -6.89) * mm, "end": v(-77.05, -6.3) * mm});
            skArc(sketch, "E68.1.1.78", {"start": v(73.15, -8.3) * mm, "mid": v(72.56, -6.89) * mm, "end": v(71.15, -6.3) * mm});
            skArc(sketch, "E68.1.1.79", {"start": v(-50.35, -8.3) * mm, "mid": v(-50.94, -6.89) * mm, "end": v(-52.35, -6.3) * mm});
            skArc(sketch, "E68.1.1.80", {"start": v(-46.45, -6.3) * mm, "mid": v(-47.86, -6.89) * mm, "end": v(-48.45, -8.3) * mm});
            skArc(sketch, "E68.1.1.81", {"start": v(97.85, -8.3) * mm, "mid": v(97.26, -6.89) * mm, "end": v(95.85, -6.3) * mm});
            skArc(sketch, "E68.1.1.82", {"start": v(23.75, -8.3) * mm, "mid": v(23.16, -6.89) * mm, "end": v(21.75, -6.3) * mm});
            skArc(sketch, "E68.1.1.83", {"start": v(48.45, -8.3) * mm, "mid": v(47.86, -6.89) * mm, "end": v(46.45, -6.3) * mm});
            skArc(sketch, "E68.1.1.84", {"start": v(27.65, -6.3) * mm, "mid": v(26.24, -6.89) * mm, "end": v(25.65, -8.3) * mm});
            skArc(sketch, "E68.1.1.85", {"start": v(52.35, -6.3) * mm, "mid": v(50.94, -6.89) * mm, "end": v(50.35, -8.3) * mm});
            skArc(sketch, "E68.1.1.86", {"start": v(-21.75, -6.3) * mm, "mid": v(-23.16, -6.89) * mm, "end": v(-23.75, -8.3) * mm});
            skArc(sketch, "E68.1.1.87", {"start": v(-0.95, -8.3) * mm, "mid": v(-1.54, -6.89) * mm, "end": v(-2.95, -6.3) * mm});
            skArc(sketch, "E68.1.1.88", {"start": v(-25.65, -8.3) * mm, "mid": v(-26.24, -6.89) * mm, "end": v(-27.65, -6.3) * mm});
            skArc(sketch, "E68.1.1.89", {"start": v(2.95, -6.3) * mm, "mid": v(1.54, -6.89) * mm, "end": v(0.95, -8.3) * mm});
            skArc(sketch, "E68.1.1.90", {"start": v(-77.05, -38.8) * mm, "mid": v(-75.64, -38.21) * mm, "end": v(-75.05, -36.8) * mm});
            skArc(sketch, "E68.1.1.91", {"start": v(50.35, -36.8) * mm, "mid": v(50.94, -38.21) * mm, "end": v(52.35, -38.8) * mm});
            skArc(sketch, "E68.1.1.92", {"start": v(-52.35, -38.8) * mm, "mid": v(-50.94, -38.21) * mm, "end": v(-50.35, -36.8) * mm});
            skArc(sketch, "E68.1.1.93", {"start": v(0.95, -36.8) * mm, "mid": v(1.54, -38.21) * mm, "end": v(2.95, -38.8) * mm});
            skArc(sketch, "E68.1.1.94", {"start": v(46.45, -38.8) * mm, "mid": v(47.86, -38.21) * mm, "end": v(48.45, -36.8) * mm});
            skArc(sketch, "E68.1.1.95", {"start": v(-73.15, -36.8) * mm, "mid": v(-72.56, -38.21) * mm, "end": v(-71.15, -38.8) * mm});
            skArc(sketch, "E68.1.1.96", {"start": v(-97.85, -36.8) * mm, "mid": v(-97.26, -38.21) * mm, "end": v(-95.85, -38.8) * mm});
            skArc(sketch, "E68.1.1.97", {"start": v(-48.45, -36.8) * mm, "mid": v(-47.86, -38.21) * mm, "end": v(-46.45, -38.8) * mm});
            skArc(sketch, "E68.1.1.98", {"start": v(-2.95, -38.8) * mm, "mid": v(-1.54, -38.21) * mm, "end": v(-0.95, -36.8) * mm});
            skArc(sketch, "E68.1.1.99", {"start": v(-48.45, -36.8) * mm, "mid": v(-47.86, -38.21) * mm, "end": v(-46.45, -38.8) * mm});
            skArc(sketch, "E68.1.1.100", {"start": v(-27.65, -38.8) * mm, "mid": v(-26.24, -38.21) * mm, "end": v(-25.65, -36.8) * mm});
            skArc(sketch, "E68.1.1.101", {"start": v(-23.75, -36.8) * mm, "mid": v(-23.16, -38.21) * mm, "end": v(-21.75, -38.8) * mm});
            skArc(sketch, "E68.1.1.102", {"start": v(0.95, -36.8) * mm, "mid": v(1.54, -38.21) * mm, "end": v(2.95, -38.8) * mm});
            skArc(sketch, "E68.1.1.103", {"start": v(50.35, -36.8) * mm, "mid": v(50.94, -38.21) * mm, "end": v(52.35, -38.8) * mm});
            skArc(sketch, "E68.1.1.104", {"start": v(-73.15, -36.8) * mm, "mid": v(-72.56, -38.21) * mm, "end": v(-71.15, -38.8) * mm});
            skArc(sketch, "E68.1.1.105", {"start": v(-97.85, -36.8) * mm, "mid": v(-97.26, -38.21) * mm, "end": v(-95.85, -38.8) * mm});
            skArc(sketch, "E68.1.1.106", {"start": v(-23.75, -36.8) * mm, "mid": v(-23.16, -38.21) * mm, "end": v(-21.75, -38.8) * mm});
            skArc(sketch, "E68.1.1.107", {"start": v(25.65, -36.8) * mm, "mid": v(26.24, -38.21) * mm, "end": v(27.65, -38.8) * mm});
            skArc(sketch, "E68.1.1.108", {"start": v(21.75, -38.8) * mm, "mid": v(23.16, -38.21) * mm, "end": v(23.75, -36.8) * mm});
            skArc(sketch, "E68.1.1.109", {"start": v(75.05, -36.8) * mm, "mid": v(75.64, -38.21) * mm, "end": v(77.05, -38.8) * mm});
            skArc(sketch, "E68.1.1.110", {"start": v(71.15, -38.8) * mm, "mid": v(72.56, -38.21) * mm, "end": v(73.15, -36.8) * mm});
            skArc(sketch, "E68.1.1.111", {"start": v(25.65, -36.8) * mm, "mid": v(26.24, -38.21) * mm, "end": v(27.65, -38.8) * mm});
            skArc(sketch, "E68.1.1.112", {"start": v(75.05, -36.8) * mm, "mid": v(75.64, -38.21) * mm, "end": v(77.05, -38.8) * mm});
            skLineSegment(sketch, "E68.1.2.0", {"start": v(-25.65, -1.6) * mm, "end": v(-25.65, 26.9) * mm});
            skPoint(sketch, "E68.1.2.1", {"position": v(25.65, -3.6) * mm});
            skLineSegment(sketch, "E68.1.2.2", {"start": v(-75.05, -1.6) * mm, "end": v(-75.05, 26.9) * mm});
            skPoint(sketch, "E68.1.2.3", {"position": v(75.05, 28.9) * mm});
            skPoint(sketch, "E68.1.2.4", {"position": v(-50.35, -3.6) * mm});
            skLineSegment(sketch, "E68.1.2.5", {"start": v(27.65, 28.9) * mm, "end": v(46.45, 28.9) * mm});
            skLineSegment(sketch, "E68.1.2.6", {"start": v(48.45, -1.6) * mm, "end": v(48.45, 26.9) * mm});
            skPoint(sketch, "E68.1.2.7", {"position": v(0.95, 28.9) * mm});
            skPoint(sketch, "E68.1.2.8", {"position": v(-73.15, -3.6) * mm});
            skLineSegment(sketch, "E68.1.2.9", {"start": v(-95.85, 28.9) * mm, "end": v(-77.05, 28.9) * mm});
            skLineSegment(sketch, "E68.1.2.10", {"start": v(-97.85, -1.6) * mm, "end": v(-97.85, 26.9) * mm});
            skLineSegment(sketch, "E68.1.2.11", {"start": v(75.05, -1.6) * mm, "end": v(75.05, 26.9) * mm});
            skLineSegment(sketch, "E68.1.2.12", {"start": v(-21.75, -3.6) * mm, "end": v(-2.95, -3.6) * mm});
            skPoint(sketch, "E68.1.2.13", {"position": v(50.35, 28.9) * mm});
            skPoint(sketch, "E68.1.2.14", {"position": v(97.85, 28.9) * mm});
            skPoint(sketch, "E68.1.2.15", {"position": v(-97.85, 28.9) * mm});
            skLineSegment(sketch, "E68.1.2.16", {"start": v(-23.75, -1.6) * mm, "end": v(-23.75, 26.9) * mm});
            skPoint(sketch, "E68.1.2.17", {"position": v(-0.95, -3.6) * mm});
            skPoint(sketch, "E68.1.2.18", {"position": v(-25.65, 28.9) * mm});
            skPoint(sketch, "E68.1.2.19", {"position": v(-25.65, -3.6) * mm});
            skLineSegment(sketch, "E68.1.2.20", {"start": v(-71.15, 28.9) * mm, "end": v(-52.35, 28.9) * mm});
            skPoint(sketch, "E68.1.2.21", {"position": v(97.85, -3.6) * mm});
            skPoint(sketch, "E68.1.2.22", {"position": v(-75.05, 28.9) * mm});
            skPoint(sketch, "E68.1.2.23", {"position": v(50.35, -3.6) * mm});
            skPoint(sketch, "E68.1.2.24", {"position": v(-48.45, 28.9) * mm});
            skLineSegment(sketch, "E68.1.2.25", {"start": v(2.95, 28.9) * mm, "end": v(21.75, 28.9) * mm});
            skPoint(sketch, "E68.1.2.26", {"position": v(-50.35, 28.9) * mm});
            skLineSegment(sketch, "E68.1.2.27", {"start": v(2.95, -3.6) * mm, "end": v(21.75, -3.6) * mm});
            skLineSegment(sketch, "E68.1.2.28", {"start": v(-73.15, -1.6) * mm, "end": v(-73.15, 26.9) * mm});
            skLineSegment(sketch, "E68.1.2.29", {"start": v(-46.45, 28.9) * mm, "end": v(-27.65, 28.9) * mm});
            skLineSegment(sketch, "E68.1.2.30", {"start": v(23.75, -1.6) * mm, "end": v(23.75, 26.9) * mm});
            skLineSegment(sketch, "E68.1.2.31", {"start": v(50.35, -1.6) * mm, "end": v(50.35, 26.9) * mm});
            skLineSegment(sketch, "E68.1.2.32", {"start": v(-46.45, -3.6) * mm, "end": v(-27.65, -3.6) * mm});
            skPoint(sketch, "E68.1.2.33", {"position": v(48.45, 28.9) * mm});
            skLineSegment(sketch, "E68.1.2.34", {"start": v(52.35, -3.6) * mm, "end": v(71.15, -3.6) * mm});
            skLineSegment(sketch, "E68.1.2.35", {"start": v(-0.95, -1.6) * mm, "end": v(-0.95, 26.9) * mm});
            skLineSegment(sketch, "E68.1.2.36", {"start": v(-48.45, -1.6) * mm, "end": v(-48.45, 26.9) * mm});
            skLineSegment(sketch, "E68.1.2.37", {"start": v(77.05, 28.9) * mm, "end": v(95.85, 28.9) * mm});
            skPoint(sketch, "E68.1.2.38", {"position": v(0.95, -3.6) * mm});
            skPoint(sketch, "E68.1.2.39", {"position": v(25.65, 28.9) * mm});
            skLineSegment(sketch, "E68.1.2.40", {"start": v(52.35, 28.9) * mm, "end": v(71.15, 28.9) * mm});
            skLineSegment(sketch, "E68.1.2.41", {"start": v(97.85, -1.6) * mm, "end": v(97.85, 26.9) * mm});
            skPoint(sketch, "E68.1.2.42", {"position": v(73.15, -3.6) * mm});
            skLineSegment(sketch, "E68.1.2.43", {"start": v(25.65, -1.6) * mm, "end": v(25.65, 26.9) * mm});
            skPoint(sketch, "E68.1.2.44", {"position": v(-73.15, 28.9) * mm});
            skPoint(sketch, "E68.1.2.45", {"position": v(23.75, 28.9) * mm});
            skLineSegment(sketch, "E68.1.2.46", {"start": v(27.65, -3.6) * mm, "end": v(46.45, -3.6) * mm});
            skLineSegment(sketch, "E68.1.2.47", {"start": v(0.95, -1.6) * mm, "end": v(0.95, 26.9) * mm});
            skLineSegment(sketch, "E68.1.2.48", {"start": v(73.15, -1.6) * mm, "end": v(73.15, 26.9) * mm});
            skPoint(sketch, "E68.1.2.49", {"position": v(48.45, -3.6) * mm});
            skPoint(sketch, "E68.1.2.50", {"position": v(-0.95, 28.9) * mm});
            skLineSegment(sketch, "E68.1.2.51", {"start": v(-71.15, -3.6) * mm, "end": v(-52.35, -3.6) * mm});
            skLineSegment(sketch, "E68.1.2.52", {"start": v(-50.35, -1.6) * mm, "end": v(-50.35, 26.9) * mm});
            skLineSegment(sketch, "E68.1.2.53", {"start": v(-21.75, 28.9) * mm, "end": v(-2.95, 28.9) * mm});
            skPoint(sketch, "E68.1.2.54", {"position": v(73.15, 28.9) * mm});
            skPoint(sketch, "E68.1.2.55", {"position": v(23.75, -3.6) * mm});
            skPoint(sketch, "E68.1.2.56", {"position": v(-48.45, -3.6) * mm});
            skPoint(sketch, "E68.1.2.57", {"position": v(-23.75, 28.9) * mm});
            skPoint(sketch, "E68.1.2.58", {"position": v(-97.85, -3.6) * mm});
            skPoint(sketch, "E68.1.2.59", {"position": v(75.05, -3.6) * mm});
            skPoint(sketch, "E68.1.2.60", {"position": v(-23.75, -3.6) * mm});
            skLineSegment(sketch, "E68.1.2.61", {"start": v(77.05, -3.6) * mm, "end": v(95.85, -3.6) * mm});
            skPoint(sketch, "E68.1.2.62", {"position": v(-23.75, -3.6) * mm});
            skPoint(sketch, "E68.1.2.63", {"position": v(25.65, -3.6) * mm});
            skPoint(sketch, "E68.1.2.64", {"position": v(0.95, -3.6) * mm});
            skPoint(sketch, "E68.1.2.65", {"position": v(-97.85, -3.6) * mm});
            skPoint(sketch, "E68.1.2.66", {"position": v(50.35, -3.6) * mm});
            skPoint(sketch, "E68.1.2.67", {"position": v(-48.45, -3.6) * mm});
            skPoint(sketch, "E68.1.2.68", {"position": v(75.05, -3.6) * mm});
            skPoint(sketch, "E68.1.2.69", {"position": v(-73.15, -3.6) * mm});
            skLineSegment(sketch, "E68.1.2.70", {"start": v(-97.85, -3.6) * mm, "end": v(-73.15, -3.6) * mm, "construction": true});
            skPoint(sketch, "E68.1.2.71", {"position": v(-75.05, -3.6) * mm});
            skLineSegment(sketch, "E68.1.2.72", {"start": v(-95.85, -3.6) * mm, "end": v(-77.05, -3.6) * mm});
            skArc(sketch, "E68.1.2.73", {"start": v(-95.85, 28.9) * mm, "mid": v(-97.26, 28.31) * mm, "end": v(-97.85, 26.9) * mm});
            skArc(sketch, "E68.1.2.74", {"start": v(77.05, 28.9) * mm, "mid": v(75.64, 28.31) * mm, "end": v(75.05, 26.9) * mm});
            skArc(sketch, "E68.1.2.75", {"start": v(95.85, -3.6) * mm, "mid": v(97.26, -3.01) * mm, "end": v(97.85, -1.6) * mm});
            skArc(sketch, "E68.1.2.76", {"start": v(-71.15, 28.9) * mm, "mid": v(-72.56, 28.31) * mm, "end": v(-73.15, 26.9) * mm});
            skArc(sketch, "E68.1.2.77", {"start": v(-75.05, 26.9) * mm, "mid": v(-75.64, 28.31) * mm, "end": v(-77.05, 28.9) * mm});
            skArc(sketch, "E68.1.2.78", {"start": v(73.15, 26.9) * mm, "mid": v(72.56, 28.31) * mm, "end": v(71.15, 28.9) * mm});
            skArc(sketch, "E68.1.2.79", {"start": v(-50.35, 26.9) * mm, "mid": v(-50.94, 28.31) * mm, "end": v(-52.35, 28.9) * mm});
            skArc(sketch, "E68.1.2.80", {"start": v(-46.45, 28.9) * mm, "mid": v(-47.86, 28.31) * mm, "end": v(-48.45, 26.9) * mm});
            skArc(sketch, "E68.1.2.81", {"start": v(97.85, 26.9) * mm, "mid": v(97.26, 28.31) * mm, "end": v(95.85, 28.9) * mm});
            skArc(sketch, "E68.1.2.82", {"start": v(23.75, 26.9) * mm, "mid": v(23.16, 28.31) * mm, "end": v(21.75, 28.9) * mm});
            skArc(sketch, "E68.1.2.83", {"start": v(48.45, 26.9) * mm, "mid": v(47.86, 28.31) * mm, "end": v(46.45, 28.9) * mm});
            skArc(sketch, "E68.1.2.84", {"start": v(27.65, 28.9) * mm, "mid": v(26.24, 28.31) * mm, "end": v(25.65, 26.9) * mm});
            skArc(sketch, "E68.1.2.85", {"start": v(52.35, 28.9) * mm, "mid": v(50.94, 28.31) * mm, "end": v(50.35, 26.9) * mm});
            skArc(sketch, "E68.1.2.86", {"start": v(-21.75, 28.9) * mm, "mid": v(-23.16, 28.31) * mm, "end": v(-23.75, 26.9) * mm});
            skArc(sketch, "E68.1.2.87", {"start": v(-0.95, 26.9) * mm, "mid": v(-1.54, 28.31) * mm, "end": v(-2.95, 28.9) * mm});
            skArc(sketch, "E68.1.2.88", {"start": v(-25.65, 26.9) * mm, "mid": v(-26.24, 28.31) * mm, "end": v(-27.65, 28.9) * mm});
            skArc(sketch, "E68.1.2.89", {"start": v(2.95, 28.9) * mm, "mid": v(1.54, 28.31) * mm, "end": v(0.95, 26.9) * mm});
            skArc(sketch, "E68.1.2.90", {"start": v(-77.05, -3.6) * mm, "mid": v(-75.64, -3.01) * mm, "end": v(-75.05, -1.6) * mm});
            skArc(sketch, "E68.1.2.91", {"start": v(50.35, -1.6) * mm, "mid": v(50.94, -3.01) * mm, "end": v(52.35, -3.6) * mm});
            skArc(sketch, "E68.1.2.92", {"start": v(-52.35, -3.6) * mm, "mid": v(-50.94, -3.01) * mm, "end": v(-50.35, -1.6) * mm});
            skArc(sketch, "E68.1.2.93", {"start": v(0.95, -1.6) * mm, "mid": v(1.54, -3.01) * mm, "end": v(2.95, -3.6) * mm});
            skArc(sketch, "E68.1.2.94", {"start": v(46.45, -3.6) * mm, "mid": v(47.86, -3.01) * mm, "end": v(48.45, -1.6) * mm});
            skArc(sketch, "E68.1.2.95", {"start": v(-73.15, -1.6) * mm, "mid": v(-72.56, -3.01) * mm, "end": v(-71.15, -3.6) * mm});
            skArc(sketch, "E68.1.2.96", {"start": v(-97.85, -1.6) * mm, "mid": v(-97.26, -3.01) * mm, "end": v(-95.85, -3.6) * mm});
            skArc(sketch, "E68.1.2.97", {"start": v(-48.45, -1.6) * mm, "mid": v(-47.86, -3.01) * mm, "end": v(-46.45, -3.6) * mm});
            skArc(sketch, "E68.1.2.98", {"start": v(-2.95, -3.6) * mm, "mid": v(-1.54, -3.01) * mm, "end": v(-0.95, -1.6) * mm});
            skArc(sketch, "E68.1.2.99", {"start": v(-48.45, -1.6) * mm, "mid": v(-47.86, -3.01) * mm, "end": v(-46.45, -3.6) * mm});
            skArc(sketch, "E68.1.2.100", {"start": v(-27.65, -3.6) * mm, "mid": v(-26.24, -3.01) * mm, "end": v(-25.65, -1.6) * mm});
            skArc(sketch, "E68.1.2.101", {"start": v(-23.75, -1.6) * mm, "mid": v(-23.16, -3.01) * mm, "end": v(-21.75, -3.6) * mm});
            skArc(sketch, "E68.1.2.102", {"start": v(0.95, -1.6) * mm, "mid": v(1.54, -3.01) * mm, "end": v(2.95, -3.6) * mm});
            skArc(sketch, "E68.1.2.103", {"start": v(50.35, -1.6) * mm, "mid": v(50.94, -3.01) * mm, "end": v(52.35, -3.6) * mm});
            skArc(sketch, "E68.1.2.104", {"start": v(-73.15, -1.6) * mm, "mid": v(-72.56, -3.01) * mm, "end": v(-71.15, -3.6) * mm});
            skArc(sketch, "E68.1.2.105", {"start": v(-97.85, -1.6) * mm, "mid": v(-97.26, -3.01) * mm, "end": v(-95.85, -3.6) * mm});
            skArc(sketch, "E68.1.2.106", {"start": v(-23.75, -1.6) * mm, "mid": v(-23.16, -3.01) * mm, "end": v(-21.75, -3.6) * mm});
            skArc(sketch, "E68.1.2.107", {"start": v(25.65, -1.6) * mm, "mid": v(26.24, -3.01) * mm, "end": v(27.65, -3.6) * mm});
            skArc(sketch, "E68.1.2.108", {"start": v(21.75, -3.6) * mm, "mid": v(23.16, -3.01) * mm, "end": v(23.75, -1.6) * mm});
            skArc(sketch, "E68.1.2.109", {"start": v(75.05, -1.6) * mm, "mid": v(75.64, -3.01) * mm, "end": v(77.05, -3.6) * mm});
            skArc(sketch, "E68.1.2.110", {"start": v(71.15, -3.6) * mm, "mid": v(72.56, -3.01) * mm, "end": v(73.15, -1.6) * mm});
            skArc(sketch, "E68.1.2.111", {"start": v(25.65, -1.6) * mm, "mid": v(26.24, -3.01) * mm, "end": v(27.65, -3.6) * mm});
            skArc(sketch, "E68.1.2.112", {"start": v(75.05, -1.6) * mm, "mid": v(75.64, -3.01) * mm, "end": v(77.05, -3.6) * mm});
            skLineSegment(sketch, "E68.1.3.0", {"start": v(-25.65, 33.6) * mm, "end": v(-25.65, 62.1) * mm});
            skPoint(sketch, "E68.1.3.1", {"position": v(25.65, 31.6) * mm});
            skLineSegment(sketch, "E68.1.3.2", {"start": v(-75.05, 33.6) * mm, "end": v(-75.05, 62.1) * mm});
            skPoint(sketch, "E68.1.3.3", {"position": v(75.05, 64.1) * mm});
            skPoint(sketch, "E68.1.3.4", {"position": v(-50.35, 31.6) * mm});
            skLineSegment(sketch, "E68.1.3.5", {"start": v(27.65, 64.1) * mm, "end": v(46.45, 64.1) * mm});
            skLineSegment(sketch, "E68.1.3.6", {"start": v(48.45, 33.6) * mm, "end": v(48.45, 62.1) * mm});
            skPoint(sketch, "E68.1.3.7", {"position": v(0.95, 64.1) * mm});
            skPoint(sketch, "E68.1.3.8", {"position": v(-73.15, 31.6) * mm});
            skLineSegment(sketch, "E68.1.3.9", {"start": v(-95.85, 64.1) * mm, "end": v(-77.05, 64.1) * mm});
            skLineSegment(sketch, "E68.1.3.10", {"start": v(-97.85, 33.6) * mm, "end": v(-97.85, 62.1) * mm});
            skLineSegment(sketch, "E68.1.3.11", {"start": v(75.05, 33.6) * mm, "end": v(75.05, 62.1) * mm});
            skLineSegment(sketch, "E68.1.3.12", {"start": v(-21.75, 31.6) * mm, "end": v(-2.95, 31.6) * mm});
            skPoint(sketch, "E68.1.3.13", {"position": v(50.35, 64.1) * mm});
            skPoint(sketch, "E68.1.3.14", {"position": v(97.85, 64.1) * mm});
            skPoint(sketch, "E68.1.3.15", {"position": v(-97.85, 64.1) * mm});
            skLineSegment(sketch, "E68.1.3.16", {"start": v(-23.75, 33.6) * mm, "end": v(-23.75, 62.1) * mm});
            skPoint(sketch, "E68.1.3.17", {"position": v(-0.95, 31.6) * mm});
            skPoint(sketch, "E68.1.3.18", {"position": v(-25.65, 64.1) * mm});
            skPoint(sketch, "E68.1.3.19", {"position": v(-25.65, 31.6) * mm});
            skLineSegment(sketch, "E68.1.3.20", {"start": v(-71.15, 64.1) * mm, "end": v(-52.35, 64.1) * mm});
            skPoint(sketch, "E68.1.3.21", {"position": v(97.85, 31.6) * mm});
            skPoint(sketch, "E68.1.3.22", {"position": v(-75.05, 64.1) * mm});
            skPoint(sketch, "E68.1.3.23", {"position": v(50.35, 31.6) * mm});
            skPoint(sketch, "E68.1.3.24", {"position": v(-48.45, 64.1) * mm});
            skLineSegment(sketch, "E68.1.3.25", {"start": v(2.95, 64.1) * mm, "end": v(21.75, 64.1) * mm});
            skPoint(sketch, "E68.1.3.26", {"position": v(-50.35, 64.1) * mm});
            skLineSegment(sketch, "E68.1.3.27", {"start": v(2.95, 31.6) * mm, "end": v(21.75, 31.6) * mm});
            skLineSegment(sketch, "E68.1.3.28", {"start": v(-73.15, 33.6) * mm, "end": v(-73.15, 62.1) * mm});
            skLineSegment(sketch, "E68.1.3.29", {"start": v(-46.45, 64.1) * mm, "end": v(-27.65, 64.1) * mm});
            skLineSegment(sketch, "E68.1.3.30", {"start": v(23.75, 33.6) * mm, "end": v(23.75, 62.1) * mm});
            skLineSegment(sketch, "E68.1.3.31", {"start": v(50.35, 33.6) * mm, "end": v(50.35, 62.1) * mm});
            skLineSegment(sketch, "E68.1.3.32", {"start": v(-46.45, 31.6) * mm, "end": v(-27.65, 31.6) * mm});
            skPoint(sketch, "E68.1.3.33", {"position": v(48.45, 64.1) * mm});
            skLineSegment(sketch, "E68.1.3.34", {"start": v(52.35, 31.6) * mm, "end": v(71.15, 31.6) * mm});
            skLineSegment(sketch, "E68.1.3.35", {"start": v(-0.95, 33.6) * mm, "end": v(-0.95, 62.1) * mm});
            skLineSegment(sketch, "E68.1.3.36", {"start": v(-48.45, 33.6) * mm, "end": v(-48.45, 62.1) * mm});
            skLineSegment(sketch, "E68.1.3.37", {"start": v(77.05, 64.1) * mm, "end": v(95.85, 64.1) * mm});
            skPoint(sketch, "E68.1.3.38", {"position": v(0.95, 31.6) * mm});
            skPoint(sketch, "E68.1.3.39", {"position": v(25.65, 64.1) * mm});
            skLineSegment(sketch, "E68.1.3.40", {"start": v(52.35, 64.1) * mm, "end": v(71.15, 64.1) * mm});
            skLineSegment(sketch, "E68.1.3.41", {"start": v(97.85, 33.6) * mm, "end": v(97.85, 62.1) * mm});
            skPoint(sketch, "E68.1.3.42", {"position": v(73.15, 31.6) * mm});
            skLineSegment(sketch, "E68.1.3.43", {"start": v(25.65, 33.6) * mm, "end": v(25.65, 62.1) * mm});
            skPoint(sketch, "E68.1.3.44", {"position": v(-73.15, 64.1) * mm});
            skPoint(sketch, "E68.1.3.45", {"position": v(23.75, 64.1) * mm});
            skLineSegment(sketch, "E68.1.3.46", {"start": v(27.65, 31.6) * mm, "end": v(46.45, 31.6) * mm});
            skLineSegment(sketch, "E68.1.3.47", {"start": v(0.95, 33.6) * mm, "end": v(0.95, 62.1) * mm});
            skLineSegment(sketch, "E68.1.3.48", {"start": v(73.15, 33.6) * mm, "end": v(73.15, 62.1) * mm});
            skPoint(sketch, "E68.1.3.49", {"position": v(48.45, 31.6) * mm});
            skPoint(sketch, "E68.1.3.50", {"position": v(-0.95, 64.1) * mm});
            skLineSegment(sketch, "E68.1.3.51", {"start": v(-71.15, 31.6) * mm, "end": v(-52.35, 31.6) * mm});
            skLineSegment(sketch, "E68.1.3.52", {"start": v(-50.35, 33.6) * mm, "end": v(-50.35, 62.1) * mm});
            skLineSegment(sketch, "E68.1.3.53", {"start": v(-21.75, 64.1) * mm, "end": v(-2.95, 64.1) * mm});
            skPoint(sketch, "E68.1.3.54", {"position": v(73.15, 64.1) * mm});
            skPoint(sketch, "E68.1.3.55", {"position": v(23.75, 31.6) * mm});
            skPoint(sketch, "E68.1.3.56", {"position": v(-48.45, 31.6) * mm});
            skPoint(sketch, "E68.1.3.57", {"position": v(-23.75, 64.1) * mm});
            skPoint(sketch, "E68.1.3.58", {"position": v(-97.85, 31.6) * mm});
            skPoint(sketch, "E68.1.3.59", {"position": v(75.05, 31.6) * mm});
            skPoint(sketch, "E68.1.3.60", {"position": v(-23.75, 31.6) * mm});
            skLineSegment(sketch, "E68.1.3.61", {"start": v(77.05, 31.6) * mm, "end": v(95.85, 31.6) * mm});
            skPoint(sketch, "E68.1.3.62", {"position": v(-23.75, 31.6) * mm});
            skPoint(sketch, "E68.1.3.63", {"position": v(25.65, 31.6) * mm});
            skPoint(sketch, "E68.1.3.64", {"position": v(0.95, 31.6) * mm});
            skPoint(sketch, "E68.1.3.65", {"position": v(-97.85, 31.6) * mm});
            skPoint(sketch, "E68.1.3.66", {"position": v(50.35, 31.6) * mm});
            skPoint(sketch, "E68.1.3.67", {"position": v(-48.45, 31.6) * mm});
            skPoint(sketch, "E68.1.3.68", {"position": v(75.05, 31.6) * mm});
            skPoint(sketch, "E68.1.3.69", {"position": v(-73.15, 31.6) * mm});
            skLineSegment(sketch, "E68.1.3.70", {"start": v(-97.85, 31.6) * mm, "end": v(-73.15, 31.6) * mm, "construction": true});
            skPoint(sketch, "E68.1.3.71", {"position": v(-75.05, 31.6) * mm});
            skLineSegment(sketch, "E68.1.3.72", {"start": v(-95.85, 31.6) * mm, "end": v(-77.05, 31.6) * mm});
            skArc(sketch, "E68.1.3.73", {"start": v(-95.85, 64.1) * mm, "mid": v(-97.26, 63.51) * mm, "end": v(-97.85, 62.1) * mm});
            skArc(sketch, "E68.1.3.74", {"start": v(77.05, 64.1) * mm, "mid": v(75.64, 63.51) * mm, "end": v(75.05, 62.1) * mm});
            skArc(sketch, "E68.1.3.75", {"start": v(95.85, 31.6) * mm, "mid": v(97.26, 32.19) * mm, "end": v(97.85, 33.6) * mm});
            skArc(sketch, "E68.1.3.76", {"start": v(-71.15, 64.1) * mm, "mid": v(-72.56, 63.51) * mm, "end": v(-73.15, 62.1) * mm});
            skArc(sketch, "E68.1.3.77", {"start": v(-75.05, 62.1) * mm, "mid": v(-75.64, 63.51) * mm, "end": v(-77.05, 64.1) * mm});
            skArc(sketch, "E68.1.3.78", {"start": v(73.15, 62.1) * mm, "mid": v(72.56, 63.51) * mm, "end": v(71.15, 64.1) * mm});
            skArc(sketch, "E68.1.3.79", {"start": v(-50.35, 62.1) * mm, "mid": v(-50.94, 63.51) * mm, "end": v(-52.35, 64.1) * mm});
            skArc(sketch, "E68.1.3.80", {"start": v(-46.45, 64.1) * mm, "mid": v(-47.86, 63.51) * mm, "end": v(-48.45, 62.1) * mm});
            skArc(sketch, "E68.1.3.81", {"start": v(97.85, 62.1) * mm, "mid": v(97.26, 63.51) * mm, "end": v(95.85, 64.1) * mm});
            skArc(sketch, "E68.1.3.82", {"start": v(23.75, 62.1) * mm, "mid": v(23.16, 63.51) * mm, "end": v(21.75, 64.1) * mm});
            skArc(sketch, "E68.1.3.83", {"start": v(48.45, 62.1) * mm, "mid": v(47.86, 63.51) * mm, "end": v(46.45, 64.1) * mm});
            skArc(sketch, "E68.1.3.84", {"start": v(27.65, 64.1) * mm, "mid": v(26.24, 63.51) * mm, "end": v(25.65, 62.1) * mm});
            skArc(sketch, "E68.1.3.85", {"start": v(52.35, 64.1) * mm, "mid": v(50.94, 63.51) * mm, "end": v(50.35, 62.1) * mm});
            skArc(sketch, "E68.1.3.86", {"start": v(-21.75, 64.1) * mm, "mid": v(-23.16, 63.51) * mm, "end": v(-23.75, 62.1) * mm});
            skArc(sketch, "E68.1.3.87", {"start": v(-0.95, 62.1) * mm, "mid": v(-1.54, 63.51) * mm, "end": v(-2.95, 64.1) * mm});
            skArc(sketch, "E68.1.3.88", {"start": v(-25.65, 62.1) * mm, "mid": v(-26.24, 63.51) * mm, "end": v(-27.65, 64.1) * mm});
            skArc(sketch, "E68.1.3.89", {"start": v(2.95, 64.1) * mm, "mid": v(1.54, 63.51) * mm, "end": v(0.95, 62.1) * mm});
            skArc(sketch, "E68.1.3.90", {"start": v(-77.05, 31.6) * mm, "mid": v(-75.64, 32.19) * mm, "end": v(-75.05, 33.6) * mm});
            skArc(sketch, "E68.1.3.91", {"start": v(50.35, 33.6) * mm, "mid": v(50.94, 32.19) * mm, "end": v(52.35, 31.6) * mm});
            skArc(sketch, "E68.1.3.92", {"start": v(-52.35, 31.6) * mm, "mid": v(-50.94, 32.19) * mm, "end": v(-50.35, 33.6) * mm});
            skArc(sketch, "E68.1.3.93", {"start": v(0.95, 33.6) * mm, "mid": v(1.54, 32.19) * mm, "end": v(2.95, 31.6) * mm});
            skArc(sketch, "E68.1.3.94", {"start": v(46.45, 31.6) * mm, "mid": v(47.86, 32.19) * mm, "end": v(48.45, 33.6) * mm});
            skArc(sketch, "E68.1.3.95", {"start": v(-73.15, 33.6) * mm, "mid": v(-72.56, 32.19) * mm, "end": v(-71.15, 31.6) * mm});
            skArc(sketch, "E68.1.3.96", {"start": v(-97.85, 33.6) * mm, "mid": v(-97.26, 32.19) * mm, "end": v(-95.85, 31.6) * mm});
            skArc(sketch, "E68.1.3.97", {"start": v(-48.45, 33.6) * mm, "mid": v(-47.86, 32.19) * mm, "end": v(-46.45, 31.6) * mm});
            skArc(sketch, "E68.1.3.98", {"start": v(-2.95, 31.6) * mm, "mid": v(-1.54, 32.19) * mm, "end": v(-0.95, 33.6) * mm});
            skArc(sketch, "E68.1.3.99", {"start": v(-48.45, 33.6) * mm, "mid": v(-47.86, 32.19) * mm, "end": v(-46.45, 31.6) * mm});
            skArc(sketch, "E68.1.3.100", {"start": v(-27.65, 31.6) * mm, "mid": v(-26.24, 32.19) * mm, "end": v(-25.65, 33.6) * mm});
            skArc(sketch, "E68.1.3.101", {"start": v(-23.75, 33.6) * mm, "mid": v(-23.16, 32.19) * mm, "end": v(-21.75, 31.6) * mm});
            skArc(sketch, "E68.1.3.102", {"start": v(0.95, 33.6) * mm, "mid": v(1.54, 32.19) * mm, "end": v(2.95, 31.6) * mm});
            skArc(sketch, "E68.1.3.103", {"start": v(50.35, 33.6) * mm, "mid": v(50.94, 32.19) * mm, "end": v(52.35, 31.6) * mm});
            skArc(sketch, "E68.1.3.104", {"start": v(-73.15, 33.6) * mm, "mid": v(-72.56, 32.19) * mm, "end": v(-71.15, 31.6) * mm});
            skArc(sketch, "E68.1.3.105", {"start": v(-97.85, 33.6) * mm, "mid": v(-97.26, 32.19) * mm, "end": v(-95.85, 31.6) * mm});
            skArc(sketch, "E68.1.3.106", {"start": v(-23.75, 33.6) * mm, "mid": v(-23.16, 32.19) * mm, "end": v(-21.75, 31.6) * mm});
            skArc(sketch, "E68.1.3.107", {"start": v(25.65, 33.6) * mm, "mid": v(26.24, 32.19) * mm, "end": v(27.65, 31.6) * mm});
            skArc(sketch, "E68.1.3.108", {"start": v(21.75, 31.6) * mm, "mid": v(23.16, 32.19) * mm, "end": v(23.75, 33.6) * mm});
            skArc(sketch, "E68.1.3.109", {"start": v(75.05, 33.6) * mm, "mid": v(75.64, 32.19) * mm, "end": v(77.05, 31.6) * mm});
            skArc(sketch, "E68.1.3.110", {"start": v(71.15, 31.6) * mm, "mid": v(72.56, 32.19) * mm, "end": v(73.15, 33.6) * mm});
            skArc(sketch, "E68.1.3.111", {"start": v(25.65, 33.6) * mm, "mid": v(26.24, 32.19) * mm, "end": v(27.65, 31.6) * mm});
            skArc(sketch, "E68.1.3.112", {"start": v(75.05, 33.6) * mm, "mid": v(75.64, 32.19) * mm, "end": v(77.05, 31.6) * mm});
            skLineSegment(sketch, "E68.2.1.0", {"start": v(-25.65, -36.8) * mm, "end": v(-25.65, -8.3) * mm});
            skPoint(sketch, "E68.2.1.1", {"position": v(25.65, -38.8) * mm});
            skLineSegment(sketch, "E68.2.1.2", {"start": v(-75.05, -36.8) * mm, "end": v(-75.05, -8.3) * mm});
            skPoint(sketch, "E68.2.1.3", {"position": v(75.05, -6.3) * mm});
            skPoint(sketch, "E68.2.1.4", {"position": v(-50.35, -38.8) * mm});
            skLineSegment(sketch, "E68.2.1.5", {"start": v(27.65, -6.3) * mm, "end": v(46.45, -6.3) * mm});
            skLineSegment(sketch, "E68.2.1.6", {"start": v(48.45, -36.8) * mm, "end": v(48.45, -8.3) * mm});
            skPoint(sketch, "E68.2.1.7", {"position": v(0.95, -6.3) * mm});
            skPoint(sketch, "E68.2.1.8", {"position": v(-73.15, -38.8) * mm});
            skLineSegment(sketch, "E68.2.1.9", {"start": v(-95.85, -6.3) * mm, "end": v(-77.05, -6.3) * mm});
            skLineSegment(sketch, "E68.2.1.10", {"start": v(-97.85, -36.8) * mm, "end": v(-97.85, -8.3) * mm});
            skLineSegment(sketch, "E68.2.1.11", {"start": v(75.05, -36.8) * mm, "end": v(75.05, -8.3) * mm});
            skLineSegment(sketch, "E68.2.1.12", {"start": v(-21.75, -38.8) * mm, "end": v(-2.95, -38.8) * mm});
            skPoint(sketch, "E68.2.1.13", {"position": v(50.35, -6.3) * mm});
            skPoint(sketch, "E68.2.1.14", {"position": v(97.85, -6.3) * mm});
            skPoint(sketch, "E68.2.1.15", {"position": v(-97.85, -6.3) * mm});
            skLineSegment(sketch, "E68.2.1.16", {"start": v(-23.75, -36.8) * mm, "end": v(-23.75, -8.3) * mm});
            skPoint(sketch, "E68.2.1.17", {"position": v(-0.95, -38.8) * mm});
            skPoint(sketch, "E68.2.1.18", {"position": v(-25.65, -6.3) * mm});
            skPoint(sketch, "E68.2.1.19", {"position": v(-25.65, -38.8) * mm});
            skLineSegment(sketch, "E68.2.1.20", {"start": v(-71.15, -6.3) * mm, "end": v(-52.35, -6.3) * mm});
            skPoint(sketch, "E68.2.1.21", {"position": v(97.85, -38.8) * mm});
            skPoint(sketch, "E68.2.1.22", {"position": v(-75.05, -6.3) * mm});
            skPoint(sketch, "E68.2.1.23", {"position": v(50.35, -38.8) * mm});
            skPoint(sketch, "E68.2.1.24", {"position": v(-48.45, -6.3) * mm});
            skLineSegment(sketch, "E68.2.1.25", {"start": v(2.95, -6.3) * mm, "end": v(21.75, -6.3) * mm});
            skPoint(sketch, "E68.2.1.26", {"position": v(-50.35, -6.3) * mm});
            skLineSegment(sketch, "E68.2.1.27", {"start": v(2.95, -38.8) * mm, "end": v(21.75, -38.8) * mm});
            skLineSegment(sketch, "E68.2.1.28", {"start": v(-73.15, -36.8) * mm, "end": v(-73.15, -8.3) * mm});
            skLineSegment(sketch, "E68.2.1.29", {"start": v(-46.45, -6.3) * mm, "end": v(-27.65, -6.3) * mm});
            skLineSegment(sketch, "E68.2.1.30", {"start": v(23.75, -36.8) * mm, "end": v(23.75, -8.3) * mm});
            skLineSegment(sketch, "E68.2.1.31", {"start": v(50.35, -36.8) * mm, "end": v(50.35, -8.3) * mm});
            skLineSegment(sketch, "E68.2.1.32", {"start": v(-46.45, -38.8) * mm, "end": v(-27.65, -38.8) * mm});
            skPoint(sketch, "E68.2.1.33", {"position": v(48.45, -6.3) * mm});
            skLineSegment(sketch, "E68.2.1.34", {"start": v(52.35, -38.8) * mm, "end": v(71.15, -38.8) * mm});
            skLineSegment(sketch, "E68.2.1.35", {"start": v(-0.95, -36.8) * mm, "end": v(-0.95, -8.3) * mm});
            skLineSegment(sketch, "E68.2.1.36", {"start": v(-48.45, -36.8) * mm, "end": v(-48.45, -8.3) * mm});
            skLineSegment(sketch, "E68.2.1.37", {"start": v(77.05, -6.3) * mm, "end": v(95.85, -6.3) * mm});
            skPoint(sketch, "E68.2.1.38", {"position": v(0.95, -38.8) * mm});
            skPoint(sketch, "E68.2.1.39", {"position": v(25.65, -6.3) * mm});
            skLineSegment(sketch, "E68.2.1.40", {"start": v(52.35, -6.3) * mm, "end": v(71.15, -6.3) * mm});
            skLineSegment(sketch, "E68.2.1.41", {"start": v(97.85, -36.8) * mm, "end": v(97.85, -8.3) * mm});
            skPoint(sketch, "E68.2.1.42", {"position": v(73.15, -38.8) * mm});
            skLineSegment(sketch, "E68.2.1.43", {"start": v(25.65, -36.8) * mm, "end": v(25.65, -8.3) * mm});
            skPoint(sketch, "E68.2.1.44", {"position": v(-73.15, -6.3) * mm});
            skPoint(sketch, "E68.2.1.45", {"position": v(23.75, -6.3) * mm});
            skLineSegment(sketch, "E68.2.1.46", {"start": v(27.65, -38.8) * mm, "end": v(46.45, -38.8) * mm});
            skLineSegment(sketch, "E68.2.1.47", {"start": v(0.95, -36.8) * mm, "end": v(0.95, -8.3) * mm});
            skLineSegment(sketch, "E68.2.1.48", {"start": v(73.15, -36.8) * mm, "end": v(73.15, -8.3) * mm});
            skPoint(sketch, "E68.2.1.49", {"position": v(48.45, -38.8) * mm});
            skPoint(sketch, "E68.2.1.50", {"position": v(-0.95, -6.3) * mm});
            skLineSegment(sketch, "E68.2.1.51", {"start": v(-71.15, -38.8) * mm, "end": v(-52.35, -38.8) * mm});
            skLineSegment(sketch, "E68.2.1.52", {"start": v(-50.35, -36.8) * mm, "end": v(-50.35, -8.3) * mm});
            skLineSegment(sketch, "E68.2.1.53", {"start": v(-21.75, -6.3) * mm, "end": v(-2.95, -6.3) * mm});
            skPoint(sketch, "E68.2.1.54", {"position": v(73.15, -6.3) * mm});
            skPoint(sketch, "E68.2.1.55", {"position": v(23.75, -38.8) * mm});
            skPoint(sketch, "E68.2.1.56", {"position": v(-48.45, -38.8) * mm});
            skPoint(sketch, "E68.2.1.57", {"position": v(-23.75, -6.3) * mm});
            skPoint(sketch, "E68.2.1.58", {"position": v(-97.85, -38.8) * mm});
            skPoint(sketch, "E68.2.1.59", {"position": v(75.05, -38.8) * mm});
            skPoint(sketch, "E68.2.1.60", {"position": v(-23.75, -38.8) * mm});
            skLineSegment(sketch, "E68.2.1.61", {"start": v(77.05, -38.8) * mm, "end": v(95.85, -38.8) * mm});
            skPoint(sketch, "E68.2.1.62", {"position": v(-23.75, -38.8) * mm});
            skPoint(sketch, "E68.2.1.63", {"position": v(25.65, -38.8) * mm});
            skPoint(sketch, "E68.2.1.64", {"position": v(0.95, -38.8) * mm});
            skPoint(sketch, "E68.2.1.65", {"position": v(-97.85, -38.8) * mm});
            skPoint(sketch, "E68.2.1.66", {"position": v(50.35, -38.8) * mm});
            skPoint(sketch, "E68.2.1.67", {"position": v(-48.45, -38.8) * mm});
            skPoint(sketch, "E68.2.1.68", {"position": v(75.05, -38.8) * mm});
            skPoint(sketch, "E68.2.1.69", {"position": v(-73.15, -38.8) * mm});
            skLineSegment(sketch, "E68.2.1.70", {"start": v(-97.85, -38.8) * mm, "end": v(-73.15, -38.8) * mm, "construction": true});
            skPoint(sketch, "E68.2.1.71", {"position": v(-75.05, -38.8) * mm});
            skLineSegment(sketch, "E68.2.1.72", {"start": v(-95.85, -38.8) * mm, "end": v(-77.05, -38.8) * mm});
            skArc(sketch, "E68.2.1.73", {"start": v(-95.85, -6.3) * mm, "mid": v(-97.26, -6.89) * mm, "end": v(-97.85, -8.3) * mm});
            skArc(sketch, "E68.2.1.74", {"start": v(77.05, -6.3) * mm, "mid": v(75.64, -6.89) * mm, "end": v(75.05, -8.3) * mm});
            skArc(sketch, "E68.2.1.75", {"start": v(95.85, -38.8) * mm, "mid": v(97.26, -38.21) * mm, "end": v(97.85, -36.8) * mm});
            skArc(sketch, "E68.2.1.76", {"start": v(-71.15, -6.3) * mm, "mid": v(-72.56, -6.89) * mm, "end": v(-73.15, -8.3) * mm});
            skArc(sketch, "E68.2.1.77", {"start": v(-75.05, -8.3) * mm, "mid": v(-75.64, -6.89) * mm, "end": v(-77.05, -6.3) * mm});
            skArc(sketch, "E68.2.1.78", {"start": v(73.15, -8.3) * mm, "mid": v(72.56, -6.89) * mm, "end": v(71.15, -6.3) * mm});
            skArc(sketch, "E68.2.1.79", {"start": v(-50.35, -8.3) * mm, "mid": v(-50.94, -6.89) * mm, "end": v(-52.35, -6.3) * mm});
            skArc(sketch, "E68.2.1.80", {"start": v(-46.45, -6.3) * mm, "mid": v(-47.86, -6.89) * mm, "end": v(-48.45, -8.3) * mm});
            skArc(sketch, "E68.2.1.81", {"start": v(97.85, -8.3) * mm, "mid": v(97.26, -6.89) * mm, "end": v(95.85, -6.3) * mm});
            skArc(sketch, "E68.2.1.82", {"start": v(23.75, -8.3) * mm, "mid": v(23.16, -6.89) * mm, "end": v(21.75, -6.3) * mm});
            skArc(sketch, "E68.2.1.83", {"start": v(48.45, -8.3) * mm, "mid": v(47.86, -6.89) * mm, "end": v(46.45, -6.3) * mm});
            skArc(sketch, "E68.2.1.84", {"start": v(27.65, -6.3) * mm, "mid": v(26.24, -6.89) * mm, "end": v(25.65, -8.3) * mm});
            skArc(sketch, "E68.2.1.85", {"start": v(52.35, -6.3) * mm, "mid": v(50.94, -6.89) * mm, "end": v(50.35, -8.3) * mm});
            skArc(sketch, "E68.2.1.86", {"start": v(-21.75, -6.3) * mm, "mid": v(-23.16, -6.89) * mm, "end": v(-23.75, -8.3) * mm});
            skArc(sketch, "E68.2.1.87", {"start": v(-0.95, -8.3) * mm, "mid": v(-1.54, -6.89) * mm, "end": v(-2.95, -6.3) * mm});
            skArc(sketch, "E68.2.1.88", {"start": v(-25.65, -8.3) * mm, "mid": v(-26.24, -6.89) * mm, "end": v(-27.65, -6.3) * mm});
            skArc(sketch, "E68.2.1.89", {"start": v(2.95, -6.3) * mm, "mid": v(1.54, -6.89) * mm, "end": v(0.95, -8.3) * mm});
            skArc(sketch, "E68.2.1.90", {"start": v(-77.05, -38.8) * mm, "mid": v(-75.64, -38.21) * mm, "end": v(-75.05, -36.8) * mm});
            skArc(sketch, "E68.2.1.91", {"start": v(50.35, -36.8) * mm, "mid": v(50.94, -38.21) * mm, "end": v(52.35, -38.8) * mm});
            skArc(sketch, "E68.2.1.92", {"start": v(-52.35, -38.8) * mm, "mid": v(-50.94, -38.21) * mm, "end": v(-50.35, -36.8) * mm});
            skArc(sketch, "E68.2.1.93", {"start": v(0.95, -36.8) * mm, "mid": v(1.54, -38.21) * mm, "end": v(2.95, -38.8) * mm});
            skArc(sketch, "E68.2.1.94", {"start": v(46.45, -38.8) * mm, "mid": v(47.86, -38.21) * mm, "end": v(48.45, -36.8) * mm});
            skArc(sketch, "E68.2.1.95", {"start": v(-73.15, -36.8) * mm, "mid": v(-72.56, -38.21) * mm, "end": v(-71.15, -38.8) * mm});
            skArc(sketch, "E68.2.1.96", {"start": v(-97.85, -36.8) * mm, "mid": v(-97.26, -38.21) * mm, "end": v(-95.85, -38.8) * mm});
            skArc(sketch, "E68.2.1.97", {"start": v(-48.45, -36.8) * mm, "mid": v(-47.86, -38.21) * mm, "end": v(-46.45, -38.8) * mm});
            skArc(sketch, "E68.2.1.98", {"start": v(-2.95, -38.8) * mm, "mid": v(-1.54, -38.21) * mm, "end": v(-0.95, -36.8) * mm});
            skArc(sketch, "E68.2.1.99", {"start": v(-48.45, -36.8) * mm, "mid": v(-47.86, -38.21) * mm, "end": v(-46.45, -38.8) * mm});
            skArc(sketch, "E68.2.1.100", {"start": v(-27.65, -38.8) * mm, "mid": v(-26.24, -38.21) * mm, "end": v(-25.65, -36.8) * mm});
            skArc(sketch, "E68.2.1.101", {"start": v(-23.75, -36.8) * mm, "mid": v(-23.16, -38.21) * mm, "end": v(-21.75, -38.8) * mm});
            skArc(sketch, "E68.2.1.102", {"start": v(0.95, -36.8) * mm, "mid": v(1.54, -38.21) * mm, "end": v(2.95, -38.8) * mm});
            skArc(sketch, "E68.2.1.103", {"start": v(50.35, -36.8) * mm, "mid": v(50.94, -38.21) * mm, "end": v(52.35, -38.8) * mm});
            skArc(sketch, "E68.2.1.104", {"start": v(-73.15, -36.8) * mm, "mid": v(-72.56, -38.21) * mm, "end": v(-71.15, -38.8) * mm});
            skArc(sketch, "E68.2.1.105", {"start": v(-97.85, -36.8) * mm, "mid": v(-97.26, -38.21) * mm, "end": v(-95.85, -38.8) * mm});
            skArc(sketch, "E68.2.1.106", {"start": v(-23.75, -36.8) * mm, "mid": v(-23.16, -38.21) * mm, "end": v(-21.75, -38.8) * mm});
            skArc(sketch, "E68.2.1.107", {"start": v(25.65, -36.8) * mm, "mid": v(26.24, -38.21) * mm, "end": v(27.65, -38.8) * mm});
            skArc(sketch, "E68.2.1.108", {"start": v(21.75, -38.8) * mm, "mid": v(23.16, -38.21) * mm, "end": v(23.75, -36.8) * mm});
            skArc(sketch, "E68.2.1.109", {"start": v(75.05, -36.8) * mm, "mid": v(75.64, -38.21) * mm, "end": v(77.05, -38.8) * mm});
            skArc(sketch, "E68.2.1.110", {"start": v(71.15, -38.8) * mm, "mid": v(72.56, -38.21) * mm, "end": v(73.15, -36.8) * mm});
            skArc(sketch, "E68.2.1.111", {"start": v(25.65, -36.8) * mm, "mid": v(26.24, -38.21) * mm, "end": v(27.65, -38.8) * mm});
            skArc(sketch, "E68.2.1.112", {"start": v(75.05, -36.8) * mm, "mid": v(75.64, -38.21) * mm, "end": v(77.05, -38.8) * mm});
            skLineSegment(sketch, "E68.2.2.0", {"start": v(-25.65, -1.6) * mm, "end": v(-25.65, 26.9) * mm});
            skPoint(sketch, "E68.2.2.1", {"position": v(25.65, -3.6) * mm});
            skLineSegment(sketch, "E68.2.2.2", {"start": v(-75.05, -1.6) * mm, "end": v(-75.05, 26.9) * mm});
            skPoint(sketch, "E68.2.2.3", {"position": v(75.05, 28.9) * mm});
            skPoint(sketch, "E68.2.2.4", {"position": v(-50.35, -3.6) * mm});
            skLineSegment(sketch, "E68.2.2.5", {"start": v(27.65, 28.9) * mm, "end": v(46.45, 28.9) * mm});
            skLineSegment(sketch, "E68.2.2.6", {"start": v(48.45, -1.6) * mm, "end": v(48.45, 26.9) * mm});
            skPoint(sketch, "E68.2.2.7", {"position": v(0.95, 28.9) * mm});
            skPoint(sketch, "E68.2.2.8", {"position": v(-73.15, -3.6) * mm});
            skLineSegment(sketch, "E68.2.2.9", {"start": v(-95.85, 28.9) * mm, "end": v(-77.05, 28.9) * mm});
            skLineSegment(sketch, "E68.2.2.10", {"start": v(-97.85, -1.6) * mm, "end": v(-97.85, 26.9) * mm});
            skLineSegment(sketch, "E68.2.2.11", {"start": v(75.05, -1.6) * mm, "end": v(75.05, 26.9) * mm});
            skLineSegment(sketch, "E68.2.2.12", {"start": v(-21.75, -3.6) * mm, "end": v(-2.95, -3.6) * mm});
            skPoint(sketch, "E68.2.2.13", {"position": v(50.35, 28.9) * mm});
            skPoint(sketch, "E68.2.2.14", {"position": v(97.85, 28.9) * mm});
            skPoint(sketch, "E68.2.2.15", {"position": v(-97.85, 28.9) * mm});
            skLineSegment(sketch, "E68.2.2.16", {"start": v(-23.75, -1.6) * mm, "end": v(-23.75, 26.9) * mm});
            skPoint(sketch, "E68.2.2.17", {"position": v(-0.95, -3.6) * mm});
            skPoint(sketch, "E68.2.2.18", {"position": v(-25.65, 28.9) * mm});
            skPoint(sketch, "E68.2.2.19", {"position": v(-25.65, -3.6) * mm});
            skLineSegment(sketch, "E68.2.2.20", {"start": v(-71.15, 28.9) * mm, "end": v(-52.35, 28.9) * mm});
            skPoint(sketch, "E68.2.2.21", {"position": v(97.85, -3.6) * mm});
            skPoint(sketch, "E68.2.2.22", {"position": v(-75.05, 28.9) * mm});
            skPoint(sketch, "E68.2.2.23", {"position": v(50.35, -3.6) * mm});
            skPoint(sketch, "E68.2.2.24", {"position": v(-48.45, 28.9) * mm});
            skLineSegment(sketch, "E68.2.2.25", {"start": v(2.95, 28.9) * mm, "end": v(21.75, 28.9) * mm});
            skPoint(sketch, "E68.2.2.26", {"position": v(-50.35, 28.9) * mm});
            skLineSegment(sketch, "E68.2.2.27", {"start": v(2.95, -3.6) * mm, "end": v(21.75, -3.6) * mm});
            skLineSegment(sketch, "E68.2.2.28", {"start": v(-73.15, -1.6) * mm, "end": v(-73.15, 26.9) * mm});
            skLineSegment(sketch, "E68.2.2.29", {"start": v(-46.45, 28.9) * mm, "end": v(-27.65, 28.9) * mm});
            skLineSegment(sketch, "E68.2.2.30", {"start": v(23.75, -1.6) * mm, "end": v(23.75, 26.9) * mm});
            skLineSegment(sketch, "E68.2.2.31", {"start": v(50.35, -1.6) * mm, "end": v(50.35, 26.9) * mm});
            skLineSegment(sketch, "E68.2.2.32", {"start": v(-46.45, -3.6) * mm, "end": v(-27.65, -3.6) * mm});
            skPoint(sketch, "E68.2.2.33", {"position": v(48.45, 28.9) * mm});
            skLineSegment(sketch, "E68.2.2.34", {"start": v(52.35, -3.6) * mm, "end": v(71.15, -3.6) * mm});
            skLineSegment(sketch, "E68.2.2.35", {"start": v(-0.95, -1.6) * mm, "end": v(-0.95, 26.9) * mm});
            skLineSegment(sketch, "E68.2.2.36", {"start": v(-48.45, -1.6) * mm, "end": v(-48.45, 26.9) * mm});
            skLineSegment(sketch, "E68.2.2.37", {"start": v(77.05, 28.9) * mm, "end": v(95.85, 28.9) * mm});
            skPoint(sketch, "E68.2.2.38", {"position": v(0.95, -3.6) * mm});
            skPoint(sketch, "E68.2.2.39", {"position": v(25.65, 28.9) * mm});
            skLineSegment(sketch, "E68.2.2.40", {"start": v(52.35, 28.9) * mm, "end": v(71.15, 28.9) * mm});
            skLineSegment(sketch, "E68.2.2.41", {"start": v(97.85, -1.6) * mm, "end": v(97.85, 26.9) * mm});
            skPoint(sketch, "E68.2.2.42", {"position": v(73.15, -3.6) * mm});
            skLineSegment(sketch, "E68.2.2.43", {"start": v(25.65, -1.6) * mm, "end": v(25.65, 26.9) * mm});
            skPoint(sketch, "E68.2.2.44", {"position": v(-73.15, 28.9) * mm});
            skPoint(sketch, "E68.2.2.45", {"position": v(23.75, 28.9) * mm});
            skLineSegment(sketch, "E68.2.2.46", {"start": v(27.65, -3.6) * mm, "end": v(46.45, -3.6) * mm});
            skLineSegment(sketch, "E68.2.2.47", {"start": v(0.95, -1.6) * mm, "end": v(0.95, 26.9) * mm});
            skLineSegment(sketch, "E68.2.2.48", {"start": v(73.15, -1.6) * mm, "end": v(73.15, 26.9) * mm});
            skPoint(sketch, "E68.2.2.49", {"position": v(48.45, -3.6) * mm});
            skPoint(sketch, "E68.2.2.50", {"position": v(-0.95, 28.9) * mm});
            skLineSegment(sketch, "E68.2.2.51", {"start": v(-71.15, -3.6) * mm, "end": v(-52.35, -3.6) * mm});
            skLineSegment(sketch, "E68.2.2.52", {"start": v(-50.35, -1.6) * mm, "end": v(-50.35, 26.9) * mm});
            skLineSegment(sketch, "E68.2.2.53", {"start": v(-21.75, 28.9) * mm, "end": v(-2.95, 28.9) * mm});
            skPoint(sketch, "E68.2.2.54", {"position": v(73.15, 28.9) * mm});
            skPoint(sketch, "E68.2.2.55", {"position": v(23.75, -3.6) * mm});
            skPoint(sketch, "E68.2.2.56", {"position": v(-48.45, -3.6) * mm});
            skPoint(sketch, "E68.2.2.57", {"position": v(-23.75, 28.9) * mm});
            skPoint(sketch, "E68.2.2.58", {"position": v(-97.85, -3.6) * mm});
            skPoint(sketch, "E68.2.2.59", {"position": v(75.05, -3.6) * mm});
            skPoint(sketch, "E68.2.2.60", {"position": v(-23.75, -3.6) * mm});
            skLineSegment(sketch, "E68.2.2.61", {"start": v(77.05, -3.6) * mm, "end": v(95.85, -3.6) * mm});
            skPoint(sketch, "E68.2.2.62", {"position": v(-23.75, -3.6) * mm});
            skPoint(sketch, "E68.2.2.63", {"position": v(25.65, -3.6) * mm});
            skPoint(sketch, "E68.2.2.64", {"position": v(0.95, -3.6) * mm});
            skPoint(sketch, "E68.2.2.65", {"position": v(-97.85, -3.6) * mm});
            skPoint(sketch, "E68.2.2.66", {"position": v(50.35, -3.6) * mm});
            skPoint(sketch, "E68.2.2.67", {"position": v(-48.45, -3.6) * mm});
            skPoint(sketch, "E68.2.2.68", {"position": v(75.05, -3.6) * mm});
            skPoint(sketch, "E68.2.2.69", {"position": v(-73.15, -3.6) * mm});
            skLineSegment(sketch, "E68.2.2.70", {"start": v(-97.85, -3.6) * mm, "end": v(-73.15, -3.6) * mm, "construction": true});
            skPoint(sketch, "E68.2.2.71", {"position": v(-75.05, -3.6) * mm});
            skLineSegment(sketch, "E68.2.2.72", {"start": v(-95.85, -3.6) * mm, "end": v(-77.05, -3.6) * mm});
            skArc(sketch, "E68.2.2.73", {"start": v(-95.85, 28.9) * mm, "mid": v(-97.26, 28.31) * mm, "end": v(-97.85, 26.9) * mm});
            skArc(sketch, "E68.2.2.74", {"start": v(77.05, 28.9) * mm, "mid": v(75.64, 28.31) * mm, "end": v(75.05, 26.9) * mm});
            skArc(sketch, "E68.2.2.75", {"start": v(95.85, -3.6) * mm, "mid": v(97.26, -3.01) * mm, "end": v(97.85, -1.6) * mm});
            skArc(sketch, "E68.2.2.76", {"start": v(-71.15, 28.9) * mm, "mid": v(-72.56, 28.31) * mm, "end": v(-73.15, 26.9) * mm});
            skArc(sketch, "E68.2.2.77", {"start": v(-75.05, 26.9) * mm, "mid": v(-75.64, 28.31) * mm, "end": v(-77.05, 28.9) * mm});
            skArc(sketch, "E68.2.2.78", {"start": v(73.15, 26.9) * mm, "mid": v(72.56, 28.31) * mm, "end": v(71.15, 28.9) * mm});
            skArc(sketch, "E68.2.2.79", {"start": v(-50.35, 26.9) * mm, "mid": v(-50.94, 28.31) * mm, "end": v(-52.35, 28.9) * mm});
            skArc(sketch, "E68.2.2.80", {"start": v(-46.45, 28.9) * mm, "mid": v(-47.86, 28.31) * mm, "end": v(-48.45, 26.9) * mm});
            skArc(sketch, "E68.2.2.81", {"start": v(97.85, 26.9) * mm, "mid": v(97.26, 28.31) * mm, "end": v(95.85, 28.9) * mm});
            skArc(sketch, "E68.2.2.82", {"start": v(23.75, 26.9) * mm, "mid": v(23.16, 28.31) * mm, "end": v(21.75, 28.9) * mm});
            skArc(sketch, "E68.2.2.83", {"start": v(48.45, 26.9) * mm, "mid": v(47.86, 28.31) * mm, "end": v(46.45, 28.9) * mm});
            skArc(sketch, "E68.2.2.84", {"start": v(27.65, 28.9) * mm, "mid": v(26.24, 28.31) * mm, "end": v(25.65, 26.9) * mm});
            skArc(sketch, "E68.2.2.85", {"start": v(52.35, 28.9) * mm, "mid": v(50.94, 28.31) * mm, "end": v(50.35, 26.9) * mm});
            skArc(sketch, "E68.2.2.86", {"start": v(-21.75, 28.9) * mm, "mid": v(-23.16, 28.31) * mm, "end": v(-23.75, 26.9) * mm});
            skArc(sketch, "E68.2.2.87", {"start": v(-0.95, 26.9) * mm, "mid": v(-1.54, 28.31) * mm, "end": v(-2.95, 28.9) * mm});
            skArc(sketch, "E68.2.2.88", {"start": v(-25.65, 26.9) * mm, "mid": v(-26.24, 28.31) * mm, "end": v(-27.65, 28.9) * mm});
            skArc(sketch, "E68.2.2.89", {"start": v(2.95, 28.9) * mm, "mid": v(1.54, 28.31) * mm, "end": v(0.95, 26.9) * mm});
            skArc(sketch, "E68.2.2.90", {"start": v(-77.05, -3.6) * mm, "mid": v(-75.64, -3.01) * mm, "end": v(-75.05, -1.6) * mm});
            skArc(sketch, "E68.2.2.91", {"start": v(50.35, -1.6) * mm, "mid": v(50.94, -3.01) * mm, "end": v(52.35, -3.6) * mm});
            skArc(sketch, "E68.2.2.92", {"start": v(-52.35, -3.6) * mm, "mid": v(-50.94, -3.01) * mm, "end": v(-50.35, -1.6) * mm});
            skArc(sketch, "E68.2.2.93", {"start": v(0.95, -1.6) * mm, "mid": v(1.54, -3.01) * mm, "end": v(2.95, -3.6) * mm});
            skArc(sketch, "E68.2.2.94", {"start": v(46.45, -3.6) * mm, "mid": v(47.86, -3.01) * mm, "end": v(48.45, -1.6) * mm});
            skArc(sketch, "E68.2.2.95", {"start": v(-73.15, -1.6) * mm, "mid": v(-72.56, -3.01) * mm, "end": v(-71.15, -3.6) * mm});
            skArc(sketch, "E68.2.2.96", {"start": v(-97.85, -1.6) * mm, "mid": v(-97.26, -3.01) * mm, "end": v(-95.85, -3.6) * mm});
            skArc(sketch, "E68.2.2.97", {"start": v(-48.45, -1.6) * mm, "mid": v(-47.86, -3.01) * mm, "end": v(-46.45, -3.6) * mm});
            skArc(sketch, "E68.2.2.98", {"start": v(-2.95, -3.6) * mm, "mid": v(-1.54, -3.01) * mm, "end": v(-0.95, -1.6) * mm});
            skArc(sketch, "E68.2.2.99", {"start": v(-48.45, -1.6) * mm, "mid": v(-47.86, -3.01) * mm, "end": v(-46.45, -3.6) * mm});
            skArc(sketch, "E68.2.2.100", {"start": v(-27.65, -3.6) * mm, "mid": v(-26.24, -3.01) * mm, "end": v(-25.65, -1.6) * mm});
            skArc(sketch, "E68.2.2.101", {"start": v(-23.75, -1.6) * mm, "mid": v(-23.16, -3.01) * mm, "end": v(-21.75, -3.6) * mm});
            skArc(sketch, "E68.2.2.102", {"start": v(0.95, -1.6) * mm, "mid": v(1.54, -3.01) * mm, "end": v(2.95, -3.6) * mm});
            skArc(sketch, "E68.2.2.103", {"start": v(50.35, -1.6) * mm, "mid": v(50.94, -3.01) * mm, "end": v(52.35, -3.6) * mm});
            skArc(sketch, "E68.2.2.104", {"start": v(-73.15, -1.6) * mm, "mid": v(-72.56, -3.01) * mm, "end": v(-71.15, -3.6) * mm});
            skArc(sketch, "E68.2.2.105", {"start": v(-97.85, -1.6) * mm, "mid": v(-97.26, -3.01) * mm, "end": v(-95.85, -3.6) * mm});
            skArc(sketch, "E68.2.2.106", {"start": v(-23.75, -1.6) * mm, "mid": v(-23.16, -3.01) * mm, "end": v(-21.75, -3.6) * mm});
            skArc(sketch, "E68.2.2.107", {"start": v(25.65, -1.6) * mm, "mid": v(26.24, -3.01) * mm, "end": v(27.65, -3.6) * mm});
            skArc(sketch, "E68.2.2.108", {"start": v(21.75, -3.6) * mm, "mid": v(23.16, -3.01) * mm, "end": v(23.75, -1.6) * mm});
            skArc(sketch, "E68.2.2.109", {"start": v(75.05, -1.6) * mm, "mid": v(75.64, -3.01) * mm, "end": v(77.05, -3.6) * mm});
            skArc(sketch, "E68.2.2.110", {"start": v(71.15, -3.6) * mm, "mid": v(72.56, -3.01) * mm, "end": v(73.15, -1.6) * mm});
            skArc(sketch, "E68.2.2.111", {"start": v(25.65, -1.6) * mm, "mid": v(26.24, -3.01) * mm, "end": v(27.65, -3.6) * mm});
            skArc(sketch, "E68.2.2.112", {"start": v(75.05, -1.6) * mm, "mid": v(75.64, -3.01) * mm, "end": v(77.05, -3.6) * mm});
            skLineSegment(sketch, "E68.2.3.0", {"start": v(-25.65, 33.6) * mm, "end": v(-25.65, 62.1) * mm});
            skPoint(sketch, "E68.2.3.1", {"position": v(25.65, 31.6) * mm});
            skLineSegment(sketch, "E68.2.3.2", {"start": v(-75.05, 33.6) * mm, "end": v(-75.05, 62.1) * mm});
            skPoint(sketch, "E68.2.3.3", {"position": v(75.05, 64.1) * mm});
            skPoint(sketch, "E68.2.3.4", {"position": v(-50.35, 31.6) * mm});
            skLineSegment(sketch, "E68.2.3.5", {"start": v(27.65, 64.1) * mm, "end": v(46.45, 64.1) * mm});
            skLineSegment(sketch, "E68.2.3.6", {"start": v(48.45, 33.6) * mm, "end": v(48.45, 62.1) * mm});
            skPoint(sketch, "E68.2.3.7", {"position": v(0.95, 64.1) * mm});
            skPoint(sketch, "E68.2.3.8", {"position": v(-73.15, 31.6) * mm});
            skLineSegment(sketch, "E68.2.3.9", {"start": v(-95.85, 64.1) * mm, "end": v(-77.05, 64.1) * mm});
            skLineSegment(sketch, "E68.2.3.10", {"start": v(-97.85, 33.6) * mm, "end": v(-97.85, 62.1) * mm});
            skLineSegment(sketch, "E68.2.3.11", {"start": v(75.05, 33.6) * mm, "end": v(75.05, 62.1) * mm});
            skLineSegment(sketch, "E68.2.3.12", {"start": v(-21.75, 31.6) * mm, "end": v(-2.95, 31.6) * mm});
            skPoint(sketch, "E68.2.3.13", {"position": v(50.35, 64.1) * mm});
            skPoint(sketch, "E68.2.3.14", {"position": v(97.85, 64.1) * mm});
            skPoint(sketch, "E68.2.3.15", {"position": v(-97.85, 64.1) * mm});
            skLineSegment(sketch, "E68.2.3.16", {"start": v(-23.75, 33.6) * mm, "end": v(-23.75, 62.1) * mm});
            skPoint(sketch, "E68.2.3.17", {"position": v(-0.95, 31.6) * mm});
            skPoint(sketch, "E68.2.3.18", {"position": v(-25.65, 64.1) * mm});
            skPoint(sketch, "E68.2.3.19", {"position": v(-25.65, 31.6) * mm});
            skLineSegment(sketch, "E68.2.3.20", {"start": v(-71.15, 64.1) * mm, "end": v(-52.35, 64.1) * mm});
            skPoint(sketch, "E68.2.3.21", {"position": v(97.85, 31.6) * mm});
            skPoint(sketch, "E68.2.3.22", {"position": v(-75.05, 64.1) * mm});
            skPoint(sketch, "E68.2.3.23", {"position": v(50.35, 31.6) * mm});
            skPoint(sketch, "E68.2.3.24", {"position": v(-48.45, 64.1) * mm});
            skLineSegment(sketch, "E68.2.3.25", {"start": v(2.95, 64.1) * mm, "end": v(21.75, 64.1) * mm});
            skPoint(sketch, "E68.2.3.26", {"position": v(-50.35, 64.1) * mm});
            skLineSegment(sketch, "E68.2.3.27", {"start": v(2.95, 31.6) * mm, "end": v(21.75, 31.6) * mm});
            skLineSegment(sketch, "E68.2.3.28", {"start": v(-73.15, 33.6) * mm, "end": v(-73.15, 62.1) * mm});
            skLineSegment(sketch, "E68.2.3.29", {"start": v(-46.45, 64.1) * mm, "end": v(-27.65, 64.1) * mm});
            skLineSegment(sketch, "E68.2.3.30", {"start": v(23.75, 33.6) * mm, "end": v(23.75, 62.1) * mm});
            skLineSegment(sketch, "E68.2.3.31", {"start": v(50.35, 33.6) * mm, "end": v(50.35, 62.1) * mm});
            skLineSegment(sketch, "E68.2.3.32", {"start": v(-46.45, 31.6) * mm, "end": v(-27.65, 31.6) * mm});
            skPoint(sketch, "E68.2.3.33", {"position": v(48.45, 64.1) * mm});
            skLineSegment(sketch, "E68.2.3.34", {"start": v(52.35, 31.6) * mm, "end": v(71.15, 31.6) * mm});
            skLineSegment(sketch, "E68.2.3.35", {"start": v(-0.95, 33.6) * mm, "end": v(-0.95, 62.1) * mm});
            skLineSegment(sketch, "E68.2.3.36", {"start": v(-48.45, 33.6) * mm, "end": v(-48.45, 62.1) * mm});
            skLineSegment(sketch, "E68.2.3.37", {"start": v(77.05, 64.1) * mm, "end": v(95.85, 64.1) * mm});
            skPoint(sketch, "E68.2.3.38", {"position": v(0.95, 31.6) * mm});
            skPoint(sketch, "E68.2.3.39", {"position": v(25.65, 64.1) * mm});
            skLineSegment(sketch, "E68.2.3.40", {"start": v(52.35, 64.1) * mm, "end": v(71.15, 64.1) * mm});
            skLineSegment(sketch, "E68.2.3.41", {"start": v(97.85, 33.6) * mm, "end": v(97.85, 62.1) * mm});
            skPoint(sketch, "E68.2.3.42", {"position": v(73.15, 31.6) * mm});
            skLineSegment(sketch, "E68.2.3.43", {"start": v(25.65, 33.6) * mm, "end": v(25.65, 62.1) * mm});
            skPoint(sketch, "E68.2.3.44", {"position": v(-73.15, 64.1) * mm});
            skPoint(sketch, "E68.2.3.45", {"position": v(23.75, 64.1) * mm});
            skLineSegment(sketch, "E68.2.3.46", {"start": v(27.65, 31.6) * mm, "end": v(46.45, 31.6) * mm});
            skLineSegment(sketch, "E68.2.3.47", {"start": v(0.95, 33.6) * mm, "end": v(0.95, 62.1) * mm});
            skLineSegment(sketch, "E68.2.3.48", {"start": v(73.15, 33.6) * mm, "end": v(73.15, 62.1) * mm});
            skPoint(sketch, "E68.2.3.49", {"position": v(48.45, 31.6) * mm});
            skPoint(sketch, "E68.2.3.50", {"position": v(-0.95, 64.1) * mm});
            skLineSegment(sketch, "E68.2.3.51", {"start": v(-71.15, 31.6) * mm, "end": v(-52.35, 31.6) * mm});
            skLineSegment(sketch, "E68.2.3.52", {"start": v(-50.35, 33.6) * mm, "end": v(-50.35, 62.1) * mm});
            skLineSegment(sketch, "E68.2.3.53", {"start": v(-21.75, 64.1) * mm, "end": v(-2.95, 64.1) * mm});
            skPoint(sketch, "E68.2.3.54", {"position": v(73.15, 64.1) * mm});
            skPoint(sketch, "E68.2.3.55", {"position": v(23.75, 31.6) * mm});
            skPoint(sketch, "E68.2.3.56", {"position": v(-48.45, 31.6) * mm});
            skPoint(sketch, "E68.2.3.57", {"position": v(-23.75, 64.1) * mm});
            skPoint(sketch, "E68.2.3.58", {"position": v(-97.85, 31.6) * mm});
            skPoint(sketch, "E68.2.3.59", {"position": v(75.05, 31.6) * mm});
            skPoint(sketch, "E68.2.3.60", {"position": v(-23.75, 31.6) * mm});
            skLineSegment(sketch, "E68.2.3.61", {"start": v(77.05, 31.6) * mm, "end": v(95.85, 31.6) * mm});
            skPoint(sketch, "E68.2.3.62", {"position": v(-23.75, 31.6) * mm});
            skPoint(sketch, "E68.2.3.63", {"position": v(25.65, 31.6) * mm});
            skPoint(sketch, "E68.2.3.64", {"position": v(0.95, 31.6) * mm});
            skPoint(sketch, "E68.2.3.65", {"position": v(-97.85, 31.6) * mm});
            skPoint(sketch, "E68.2.3.66", {"position": v(50.35, 31.6) * mm});
            skPoint(sketch, "E68.2.3.67", {"position": v(-48.45, 31.6) * mm});
            skPoint(sketch, "E68.2.3.68", {"position": v(75.05, 31.6) * mm});
            skPoint(sketch, "E68.2.3.69", {"position": v(-73.15, 31.6) * mm});
            skLineSegment(sketch, "E68.2.3.70", {"start": v(-97.85, 31.6) * mm, "end": v(-73.15, 31.6) * mm, "construction": true});
            skPoint(sketch, "E68.2.3.71", {"position": v(-75.05, 31.6) * mm});
            skLineSegment(sketch, "E68.2.3.72", {"start": v(-95.85, 31.6) * mm, "end": v(-77.05, 31.6) * mm});
            skArc(sketch, "E68.2.3.73", {"start": v(-95.85, 64.1) * mm, "mid": v(-97.26, 63.51) * mm, "end": v(-97.85, 62.1) * mm});
            skArc(sketch, "E68.2.3.74", {"start": v(77.05, 64.1) * mm, "mid": v(75.64, 63.51) * mm, "end": v(75.05, 62.1) * mm});
            skArc(sketch, "E68.2.3.75", {"start": v(95.85, 31.6) * mm, "mid": v(97.26, 32.19) * mm, "end": v(97.85, 33.6) * mm});
            skArc(sketch, "E68.2.3.76", {"start": v(-71.15, 64.1) * mm, "mid": v(-72.56, 63.51) * mm, "end": v(-73.15, 62.1) * mm});
            skArc(sketch, "E68.2.3.77", {"start": v(-75.05, 62.1) * mm, "mid": v(-75.64, 63.51) * mm, "end": v(-77.05, 64.1) * mm});
            skArc(sketch, "E68.2.3.78", {"start": v(73.15, 62.1) * mm, "mid": v(72.56, 63.51) * mm, "end": v(71.15, 64.1) * mm});
            skArc(sketch, "E68.2.3.79", {"start": v(-50.35, 62.1) * mm, "mid": v(-50.94, 63.51) * mm, "end": v(-52.35, 64.1) * mm});
            skArc(sketch, "E68.2.3.80", {"start": v(-46.45, 64.1) * mm, "mid": v(-47.86, 63.51) * mm, "end": v(-48.45, 62.1) * mm});
            skArc(sketch, "E68.2.3.81", {"start": v(97.85, 62.1) * mm, "mid": v(97.26, 63.51) * mm, "end": v(95.85, 64.1) * mm});
            skArc(sketch, "E68.2.3.82", {"start": v(23.75, 62.1) * mm, "mid": v(23.16, 63.51) * mm, "end": v(21.75, 64.1) * mm});
            skArc(sketch, "E68.2.3.83", {"start": v(48.45, 62.1) * mm, "mid": v(47.86, 63.51) * mm, "end": v(46.45, 64.1) * mm});
            skArc(sketch, "E68.2.3.84", {"start": v(27.65, 64.1) * mm, "mid": v(26.24, 63.51) * mm, "end": v(25.65, 62.1) * mm});
            skArc(sketch, "E68.2.3.85", {"start": v(52.35, 64.1) * mm, "mid": v(50.94, 63.51) * mm, "end": v(50.35, 62.1) * mm});
            skArc(sketch, "E68.2.3.86", {"start": v(-21.75, 64.1) * mm, "mid": v(-23.16, 63.51) * mm, "end": v(-23.75, 62.1) * mm});
            skArc(sketch, "E68.2.3.87", {"start": v(-0.95, 62.1) * mm, "mid": v(-1.54, 63.51) * mm, "end": v(-2.95, 64.1) * mm});
            skArc(sketch, "E68.2.3.88", {"start": v(-25.65, 62.1) * mm, "mid": v(-26.24, 63.51) * mm, "end": v(-27.65, 64.1) * mm});
            skArc(sketch, "E68.2.3.89", {"start": v(2.95, 64.1) * mm, "mid": v(1.54, 63.51) * mm, "end": v(0.95, 62.1) * mm});
            skArc(sketch, "E68.2.3.90", {"start": v(-77.05, 31.6) * mm, "mid": v(-75.64, 32.19) * mm, "end": v(-75.05, 33.6) * mm});
            skArc(sketch, "E68.2.3.91", {"start": v(50.35, 33.6) * mm, "mid": v(50.94, 32.19) * mm, "end": v(52.35, 31.6) * mm});
            skArc(sketch, "E68.2.3.92", {"start": v(-52.35, 31.6) * mm, "mid": v(-50.94, 32.19) * mm, "end": v(-50.35, 33.6) * mm});
            skArc(sketch, "E68.2.3.93", {"start": v(0.95, 33.6) * mm, "mid": v(1.54, 32.19) * mm, "end": v(2.95, 31.6) * mm});
            skArc(sketch, "E68.2.3.94", {"start": v(46.45, 31.6) * mm, "mid": v(47.86, 32.19) * mm, "end": v(48.45, 33.6) * mm});
            skArc(sketch, "E68.2.3.95", {"start": v(-73.15, 33.6) * mm, "mid": v(-72.56, 32.19) * mm, "end": v(-71.15, 31.6) * mm});
            skArc(sketch, "E68.2.3.96", {"start": v(-97.85, 33.6) * mm, "mid": v(-97.26, 32.19) * mm, "end": v(-95.85, 31.6) * mm});
            skArc(sketch, "E68.2.3.97", {"start": v(-48.45, 33.6) * mm, "mid": v(-47.86, 32.19) * mm, "end": v(-46.45, 31.6) * mm});
            skArc(sketch, "E68.2.3.98", {"start": v(-2.95, 31.6) * mm, "mid": v(-1.54, 32.19) * mm, "end": v(-0.95, 33.6) * mm});
            skArc(sketch, "E68.2.3.99", {"start": v(-48.45, 33.6) * mm, "mid": v(-47.86, 32.19) * mm, "end": v(-46.45, 31.6) * mm});
            skArc(sketch, "E68.2.3.100", {"start": v(-27.65, 31.6) * mm, "mid": v(-26.24, 32.19) * mm, "end": v(-25.65, 33.6) * mm});
            skArc(sketch, "E68.2.3.101", {"start": v(-23.75, 33.6) * mm, "mid": v(-23.16, 32.19) * mm, "end": v(-21.75, 31.6) * mm});
            skArc(sketch, "E68.2.3.102", {"start": v(0.95, 33.6) * mm, "mid": v(1.54, 32.19) * mm, "end": v(2.95, 31.6) * mm});
            skArc(sketch, "E68.2.3.103", {"start": v(50.35, 33.6) * mm, "mid": v(50.94, 32.19) * mm, "end": v(52.35, 31.6) * mm});
            skArc(sketch, "E68.2.3.104", {"start": v(-73.15, 33.6) * mm, "mid": v(-72.56, 32.19) * mm, "end": v(-71.15, 31.6) * mm});
            skArc(sketch, "E68.2.3.105", {"start": v(-97.85, 33.6) * mm, "mid": v(-97.26, 32.19) * mm, "end": v(-95.85, 31.6) * mm});
            skArc(sketch, "E68.2.3.106", {"start": v(-23.75, 33.6) * mm, "mid": v(-23.16, 32.19) * mm, "end": v(-21.75, 31.6) * mm});
            skArc(sketch, "E68.2.3.107", {"start": v(25.65, 33.6) * mm, "mid": v(26.24, 32.19) * mm, "end": v(27.65, 31.6) * mm});
            skArc(sketch, "E68.2.3.108", {"start": v(21.75, 31.6) * mm, "mid": v(23.16, 32.19) * mm, "end": v(23.75, 33.6) * mm});
            skArc(sketch, "E68.2.3.109", {"start": v(75.05, 33.6) * mm, "mid": v(75.64, 32.19) * mm, "end": v(77.05, 31.6) * mm});
            skArc(sketch, "E68.2.3.110", {"start": v(71.15, 31.6) * mm, "mid": v(72.56, 32.19) * mm, "end": v(73.15, 33.6) * mm});
            skArc(sketch, "E68.2.3.111", {"start": v(25.65, 33.6) * mm, "mid": v(26.24, 32.19) * mm, "end": v(27.65, 31.6) * mm});
            skArc(sketch, "E68.2.3.112", {"start": v(75.05, 33.6) * mm, "mid": v(75.64, 32.19) * mm, "end": v(77.05, 31.6) * mm});
            skLineSegment(sketch, "E68.direction1", {"start": v(-97.85, -74) * mm, "end": v(-97.85, -74) * mm});
            skLineSegment(sketch, "E68.direction2", {"start": v(-97.85, -74) * mm, "end": v(-97.85, -38.8) * mm, "construction": true});
            skPoint(sketch, "E69.endSnap0", {"position": v(97.85, 47.85) * mm});
            skLineSegment(sketch, "E70", {"start": v(-95.85, 66.8) * mm, "end": v(95.85, 66.8) * mm});
            skLineSegment(sketch, "E71", {"start": v(-97.85, 72) * mm, "end": v(-97.85, 68.8) * mm});
            skLineSegment(sketch, "E72", {"start": v(97.85, 72) * mm, "end": v(97.85, 68.8) * mm});
            skPoint(sketch, "E73.visualSharp", {"position": v(97.85, 74) * mm});
            skArc(sketch, "E73.filletArc", {"start": v(97.85, 72) * mm, "mid": v(97.26, 73.41) * mm, "end": v(95.85, 74) * mm});
            skPoint(sketch, "E74.visualSharp", {"position": v(97.85, 66.8) * mm});
            skArc(sketch, "E74.filletArc", {"start": v(95.85, 66.8) * mm, "mid": v(97.26, 67.39) * mm, "end": v(97.85, 68.8) * mm});
            skPoint(sketch, "E75.visualSharp", {"position": v(-97.85, 66.8) * mm});
            skArc(sketch, "E75.filletArc", {"start": v(-97.85, 68.8) * mm, "mid": v(-97.26, 67.39) * mm, "end": v(-95.85, 66.8) * mm});
            skPoint(sketch, "E76.visualSharp", {"position": v(-97.85, 74) * mm});
            skArc(sketch, "E76.filletArc", {"start": v(-95.85, 74) * mm, "mid": v(-97.26, 73.41) * mm, "end": v(-97.85, 72) * mm});
            skSolve(sketch);
        }
        {
            var Q0;
            Q0 = qSketchRegion(id + "F6", true);
            extrude(context, id + "F7", {"entities" : qUnion([Q0]), "operationType" : NewBodyOperationType.REMOVE, "oppositeDirection" : true, "depth" : 4 * mm, "offsetDistance" : 25 * mm});
        }
    });
